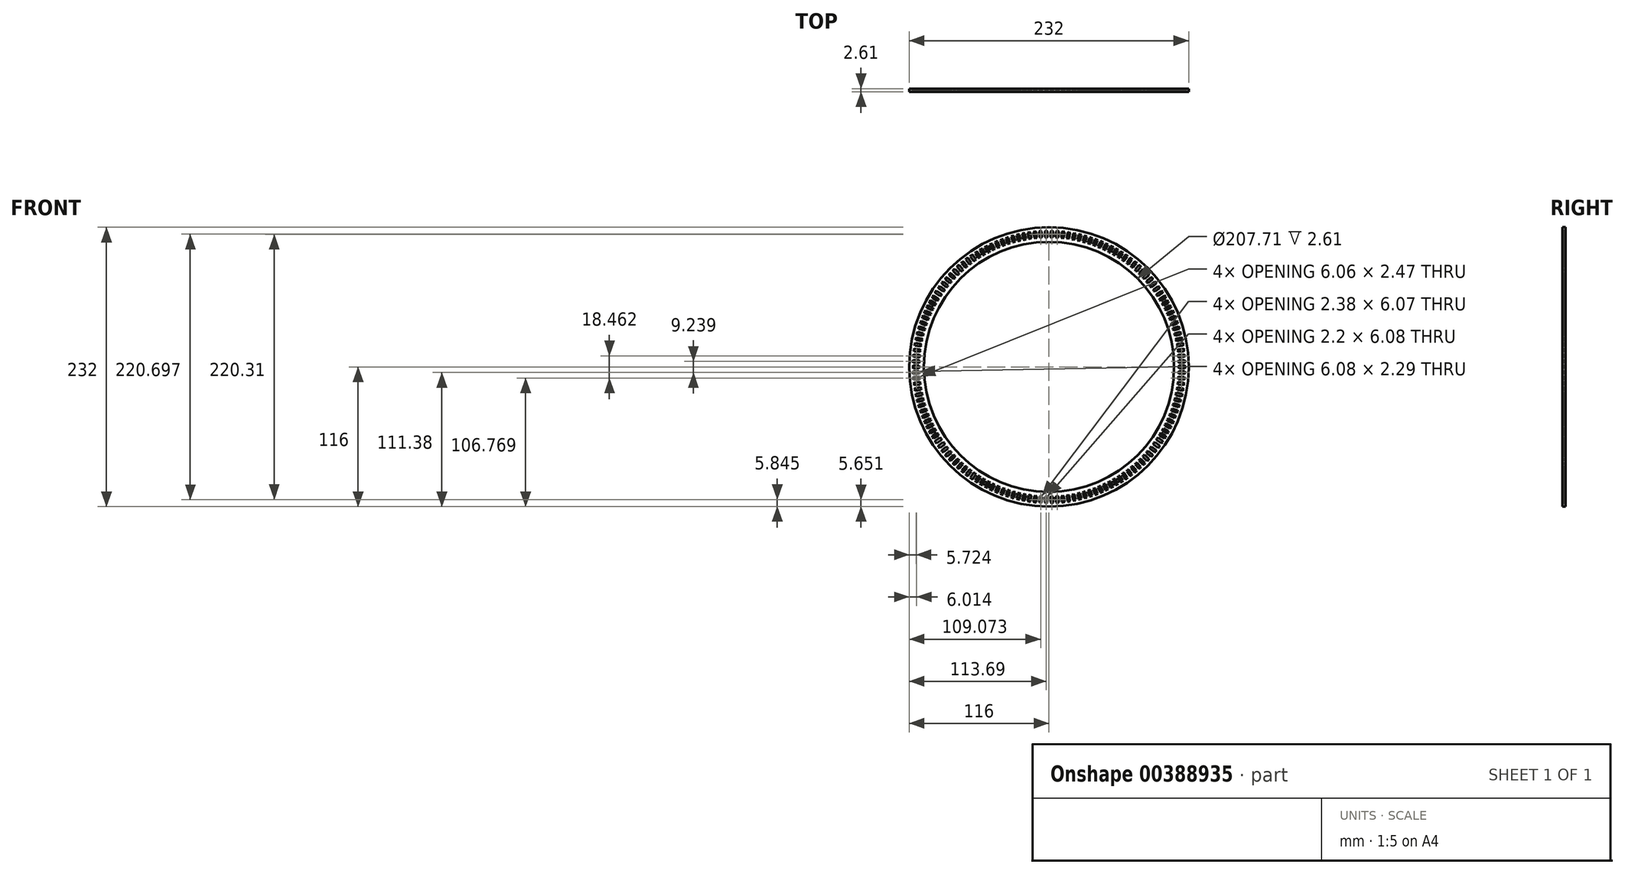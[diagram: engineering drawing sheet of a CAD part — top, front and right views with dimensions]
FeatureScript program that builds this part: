
annotation { "Feature Type Name" : "Feature", "Feature Type Description" : "" }
export const myFeature = defineFeature(function(context is Context, id is Id, definition is map)
    precondition{}
    {
        {
            var Q0;
            Q0=qCreatedBy(makeId("Front.planeOp"),FACE);
            var sketch = newSketch(context, id + "F0", { "sketchPlane" : qUnion([Q0])});
            skCircle(sketch, "E0", {"center": v(0, 0) * mm, "radius": 44.45 * mm});
            skCircle(sketch, "E1", {"center": v(0, 0) * mm, "radius": 39.8 * mm});
            skSolve(sketch);
        }
        {
            var Q0;
            Q0=makeQuery(id+"F0.imprint","IMPRINT",FACE,{"disambiguationData":[TD([[makeQuery(id+"F0.imprint","IMPRINT",EDGE,{"derivedFrom":sQuery(id+"F0.wireOp",EDGE,"E0")}),1.0]])]});
            extrude(context, id + "F1", {"entities" : qUnion([Q0]), "oppositeDirection" : true, "depth" : 1 * mm});
        }
        {
            var Q0;
            Q0=qCreatedBy(makeId("Front.planeOp"),FACE);
            var sketch = newSketch(context, id + "F2", { "sketchPlane" : qUnion([Q0])});
            skLineSegment(sketch, "E2", {"start": v(-43.11, 0.4) * mm, "end": v(-43.45, 0) * mm});
            skLineSegment(sketch, "E3", {"start": v(-41.42, 0.4) * mm, "end": v(-41.12, 0) * mm});
            skLineSegment(sketch, "E4", {"start": v(-41.12, 0) * mm, "end": v(-41.42, -0.4) * mm});
            skLineSegment(sketch, "E5", {"start": v(-43.45, 0) * mm, "end": v(-43.11, -0.4) * mm});
            skLineSegment(sketch, "E6", {"start": v(-43.11, 0.4) * mm, "end": v(-41.42, 0.4) * mm});
            skLineSegment(sketch, "E7", {"start": v(-41.42, -0.4) * mm, "end": v(-43.11, -0.4) * mm});
            skSolve(sketch);
        }
        {
            var Q0;
            Q0=qSketchRegion(id+"F2",true);
            extrude(context, id + "F3", {"entities" : qUnion([Q0]), "oppositeDirection" : true, "depth" : 1 * mm});
        }
        {
            var Q0;
            Q0=makeQuery(id+"F3.opExtrude","SWEPT_BODY",BODY,{"disambiguationData":[OSD([sQuery(id+"F2.wireOp",EDGE,"E2"),sQuery(id+"F2.wireOp",EDGE,"E3"),sQuery(id+"F2.wireOp",EDGE,"E4"),sQuery(id+"F2.wireOp",EDGE,"E5"),sQuery(id+"F2.wireOp",EDGE,"E6"),sQuery(id+"F2.wireOp",EDGE,"E7")])]});
            var Q1;
            Q1=sQuery(id+"F0.wireOp",EDGE,"E1");
            circularPattern(context, id + "F4", {"entities" : qUnion([Q0]), "axis" : qUnion([Q1]), "angle" : 360 * degree, "instanceCount" : 150, "equalSpace" : true});
        }
        {
            var Q0;
            Q0=makeQuery(id+"F4.opPattern","COPY",BODY,{"derivedFrom":makeQuery(id+"F3.opExtrude","SWEPT_BODY",BODY,{"disambiguationData":[OSD([sQuery(id+"F2.wireOp",EDGE,"E2"),sQuery(id+"F2.wireOp",EDGE,"E3"),sQuery(id+"F2.wireOp",EDGE,"E4"),sQuery(id+"F2.wireOp",EDGE,"E5"),sQuery(id+"F2.wireOp",EDGE,"E6"),sQuery(id+"F2.wireOp",EDGE,"E7")])]}),"instanceName":"5"});
            var Q1;
            Q1=makeQuery(id+"F4.opPattern","COPY",BODY,{"derivedFrom":makeQuery(id+"F3.opExtrude","SWEPT_BODY",BODY,{"disambiguationData":[OSD([sQuery(id+"F2.wireOp",EDGE,"E2"),sQuery(id+"F2.wireOp",EDGE,"E3"),sQuery(id+"F2.wireOp",EDGE,"E4"),sQuery(id+"F2.wireOp",EDGE,"E5"),sQuery(id+"F2.wireOp",EDGE,"E6"),sQuery(id+"F2.wireOp",EDGE,"E7")])]}),"instanceName":"6"});
            var Q2;
            Q2=makeQuery(id+"F4.opPattern","COPY",BODY,{"derivedFrom":makeQuery(id+"F3.opExtrude","SWEPT_BODY",BODY,{"disambiguationData":[OSD([sQuery(id+"F2.wireOp",EDGE,"E2"),sQuery(id+"F2.wireOp",EDGE,"E3"),sQuery(id+"F2.wireOp",EDGE,"E4"),sQuery(id+"F2.wireOp",EDGE,"E5"),sQuery(id+"F2.wireOp",EDGE,"E6"),sQuery(id+"F2.wireOp",EDGE,"E7")])]}),"instanceName":"4"});
            var Q3;
            Q3=makeQuery(id+"F4.opPattern","COPY",BODY,{"derivedFrom":makeQuery(id+"F3.opExtrude","SWEPT_BODY",BODY,{"disambiguationData":[OSD([sQuery(id+"F2.wireOp",EDGE,"E2"),sQuery(id+"F2.wireOp",EDGE,"E3"),sQuery(id+"F2.wireOp",EDGE,"E4"),sQuery(id+"F2.wireOp",EDGE,"E5"),sQuery(id+"F2.wireOp",EDGE,"E6"),sQuery(id+"F2.wireOp",EDGE,"E7")])]}),"instanceName":"23"});
            var Q4;
            Q4=makeQuery(id+"F4.opPattern","COPY",BODY,{"derivedFrom":makeQuery(id+"F3.opExtrude","SWEPT_BODY",BODY,{"disambiguationData":[OSD([sQuery(id+"F2.wireOp",EDGE,"E2"),sQuery(id+"F2.wireOp",EDGE,"E3"),sQuery(id+"F2.wireOp",EDGE,"E4"),sQuery(id+"F2.wireOp",EDGE,"E5"),sQuery(id+"F2.wireOp",EDGE,"E6"),sQuery(id+"F2.wireOp",EDGE,"E7")])]}),"instanceName":"21"});
            var Q5;
            Q5=makeQuery(id+"F4.opPattern","COPY",BODY,{"derivedFrom":makeQuery(id+"F3.opExtrude","SWEPT_BODY",BODY,{"disambiguationData":[OSD([sQuery(id+"F2.wireOp",EDGE,"E2"),sQuery(id+"F2.wireOp",EDGE,"E3"),sQuery(id+"F2.wireOp",EDGE,"E4"),sQuery(id+"F2.wireOp",EDGE,"E5"),sQuery(id+"F2.wireOp",EDGE,"E6"),sQuery(id+"F2.wireOp",EDGE,"E7")])]}),"instanceName":"24"});
            var Q6;
            Q6=makeQuery(id+"F4.opPattern","COPY",BODY,{"derivedFrom":makeQuery(id+"F3.opExtrude","SWEPT_BODY",BODY,{"disambiguationData":[OSD([sQuery(id+"F2.wireOp",EDGE,"E2"),sQuery(id+"F2.wireOp",EDGE,"E3"),sQuery(id+"F2.wireOp",EDGE,"E4"),sQuery(id+"F2.wireOp",EDGE,"E5"),sQuery(id+"F2.wireOp",EDGE,"E6"),sQuery(id+"F2.wireOp",EDGE,"E7")])]}),"instanceName":"22"});
            var Q7;
            Q7=makeQuery(id+"F4.opPattern","COPY",BODY,{"derivedFrom":makeQuery(id+"F3.opExtrude","SWEPT_BODY",BODY,{"disambiguationData":[OSD([sQuery(id+"F2.wireOp",EDGE,"E2"),sQuery(id+"F2.wireOp",EDGE,"E3"),sQuery(id+"F2.wireOp",EDGE,"E4"),sQuery(id+"F2.wireOp",EDGE,"E5"),sQuery(id+"F2.wireOp",EDGE,"E6"),sQuery(id+"F2.wireOp",EDGE,"E7")])]}),"instanceName":"20"});
            var Q8;
            Q8=makeQuery(id+"F4.opPattern","COPY",BODY,{"derivedFrom":makeQuery(id+"F3.opExtrude","SWEPT_BODY",BODY,{"disambiguationData":[OSD([sQuery(id+"F2.wireOp",EDGE,"E2"),sQuery(id+"F2.wireOp",EDGE,"E3"),sQuery(id+"F2.wireOp",EDGE,"E4"),sQuery(id+"F2.wireOp",EDGE,"E5"),sQuery(id+"F2.wireOp",EDGE,"E6"),sQuery(id+"F2.wireOp",EDGE,"E7")])]}),"instanceName":"19"});
            var Q9;
            Q9=makeQuery(id+"F4.opPattern","COPY",BODY,{"derivedFrom":makeQuery(id+"F3.opExtrude","SWEPT_BODY",BODY,{"disambiguationData":[OSD([sQuery(id+"F2.wireOp",EDGE,"E2"),sQuery(id+"F2.wireOp",EDGE,"E3"),sQuery(id+"F2.wireOp",EDGE,"E4"),sQuery(id+"F2.wireOp",EDGE,"E5"),sQuery(id+"F2.wireOp",EDGE,"E6"),sQuery(id+"F2.wireOp",EDGE,"E7")])]}),"instanceName":"18"});
            var Q10;
            Q10=makeQuery(id+"F4.opPattern","COPY",BODY,{"derivedFrom":makeQuery(id+"F3.opExtrude","SWEPT_BODY",BODY,{"disambiguationData":[OSD([sQuery(id+"F2.wireOp",EDGE,"E2"),sQuery(id+"F2.wireOp",EDGE,"E3"),sQuery(id+"F2.wireOp",EDGE,"E4"),sQuery(id+"F2.wireOp",EDGE,"E5"),sQuery(id+"F2.wireOp",EDGE,"E6"),sQuery(id+"F2.wireOp",EDGE,"E7")])]}),"instanceName":"17"});
            var Q11;
            Q11=makeQuery(id+"F4.opPattern","COPY",BODY,{"derivedFrom":makeQuery(id+"F3.opExtrude","SWEPT_BODY",BODY,{"disambiguationData":[OSD([sQuery(id+"F2.wireOp",EDGE,"E2"),sQuery(id+"F2.wireOp",EDGE,"E3"),sQuery(id+"F2.wireOp",EDGE,"E4"),sQuery(id+"F2.wireOp",EDGE,"E5"),sQuery(id+"F2.wireOp",EDGE,"E6"),sQuery(id+"F2.wireOp",EDGE,"E7")])]}),"instanceName":"16"});
            var Q12;
            Q12=makeQuery(id+"F4.opPattern","COPY",BODY,{"derivedFrom":makeQuery(id+"F3.opExtrude","SWEPT_BODY",BODY,{"disambiguationData":[OSD([sQuery(id+"F2.wireOp",EDGE,"E2"),sQuery(id+"F2.wireOp",EDGE,"E3"),sQuery(id+"F2.wireOp",EDGE,"E4"),sQuery(id+"F2.wireOp",EDGE,"E5"),sQuery(id+"F2.wireOp",EDGE,"E6"),sQuery(id+"F2.wireOp",EDGE,"E7")])]}),"instanceName":"15"});
            var Q13;
            Q13=makeQuery(id+"F4.opPattern","COPY",BODY,{"derivedFrom":makeQuery(id+"F3.opExtrude","SWEPT_BODY",BODY,{"disambiguationData":[OSD([sQuery(id+"F2.wireOp",EDGE,"E2"),sQuery(id+"F2.wireOp",EDGE,"E3"),sQuery(id+"F2.wireOp",EDGE,"E4"),sQuery(id+"F2.wireOp",EDGE,"E5"),sQuery(id+"F2.wireOp",EDGE,"E6"),sQuery(id+"F2.wireOp",EDGE,"E7")])]}),"instanceName":"14"});
            var Q14;
            Q14=makeQuery(id+"F4.opPattern","COPY",BODY,{"derivedFrom":makeQuery(id+"F3.opExtrude","SWEPT_BODY",BODY,{"disambiguationData":[OSD([sQuery(id+"F2.wireOp",EDGE,"E2"),sQuery(id+"F2.wireOp",EDGE,"E3"),sQuery(id+"F2.wireOp",EDGE,"E4"),sQuery(id+"F2.wireOp",EDGE,"E5"),sQuery(id+"F2.wireOp",EDGE,"E6"),sQuery(id+"F2.wireOp",EDGE,"E7")])]}),"instanceName":"13"});
            var Q15;
            Q15=makeQuery(id+"F4.opPattern","COPY",BODY,{"derivedFrom":makeQuery(id+"F3.opExtrude","SWEPT_BODY",BODY,{"disambiguationData":[OSD([sQuery(id+"F2.wireOp",EDGE,"E2"),sQuery(id+"F2.wireOp",EDGE,"E3"),sQuery(id+"F2.wireOp",EDGE,"E4"),sQuery(id+"F2.wireOp",EDGE,"E5"),sQuery(id+"F2.wireOp",EDGE,"E6"),sQuery(id+"F2.wireOp",EDGE,"E7")])]}),"instanceName":"12"});
            var Q16;
            Q16=makeQuery(id+"F4.opPattern","COPY",BODY,{"derivedFrom":makeQuery(id+"F3.opExtrude","SWEPT_BODY",BODY,{"disambiguationData":[OSD([sQuery(id+"F2.wireOp",EDGE,"E2"),sQuery(id+"F2.wireOp",EDGE,"E3"),sQuery(id+"F2.wireOp",EDGE,"E4"),sQuery(id+"F2.wireOp",EDGE,"E5"),sQuery(id+"F2.wireOp",EDGE,"E6"),sQuery(id+"F2.wireOp",EDGE,"E7")])]}),"instanceName":"11"});
            var Q17;
            Q17=makeQuery(id+"F4.opPattern","COPY",BODY,{"derivedFrom":makeQuery(id+"F3.opExtrude","SWEPT_BODY",BODY,{"disambiguationData":[OSD([sQuery(id+"F2.wireOp",EDGE,"E2"),sQuery(id+"F2.wireOp",EDGE,"E3"),sQuery(id+"F2.wireOp",EDGE,"E4"),sQuery(id+"F2.wireOp",EDGE,"E5"),sQuery(id+"F2.wireOp",EDGE,"E6"),sQuery(id+"F2.wireOp",EDGE,"E7")])]}),"instanceName":"10"});
            var Q18;
            Q18=makeQuery(id+"F4.opPattern","COPY",BODY,{"derivedFrom":makeQuery(id+"F3.opExtrude","SWEPT_BODY",BODY,{"disambiguationData":[OSD([sQuery(id+"F2.wireOp",EDGE,"E2"),sQuery(id+"F2.wireOp",EDGE,"E3"),sQuery(id+"F2.wireOp",EDGE,"E4"),sQuery(id+"F2.wireOp",EDGE,"E5"),sQuery(id+"F2.wireOp",EDGE,"E6"),sQuery(id+"F2.wireOp",EDGE,"E7")])]}),"instanceName":"9"});
            var Q19;
            Q19=makeQuery(id+"F4.opPattern","COPY",BODY,{"derivedFrom":makeQuery(id+"F3.opExtrude","SWEPT_BODY",BODY,{"disambiguationData":[OSD([sQuery(id+"F2.wireOp",EDGE,"E2"),sQuery(id+"F2.wireOp",EDGE,"E3"),sQuery(id+"F2.wireOp",EDGE,"E4"),sQuery(id+"F2.wireOp",EDGE,"E5"),sQuery(id+"F2.wireOp",EDGE,"E6"),sQuery(id+"F2.wireOp",EDGE,"E7")])]}),"instanceName":"8"});
            var Q20;
            Q20=makeQuery(id+"F4.opPattern","COPY",BODY,{"derivedFrom":makeQuery(id+"F3.opExtrude","SWEPT_BODY",BODY,{"disambiguationData":[OSD([sQuery(id+"F2.wireOp",EDGE,"E2"),sQuery(id+"F2.wireOp",EDGE,"E3"),sQuery(id+"F2.wireOp",EDGE,"E4"),sQuery(id+"F2.wireOp",EDGE,"E5"),sQuery(id+"F2.wireOp",EDGE,"E6"),sQuery(id+"F2.wireOp",EDGE,"E7")])]}),"instanceName":"7"});
            var Q21;
            Q21=makeQuery(id+"F4.opPattern","COPY",BODY,{"derivedFrom":makeQuery(id+"F3.opExtrude","SWEPT_BODY",BODY,{"disambiguationData":[OSD([sQuery(id+"F2.wireOp",EDGE,"E2"),sQuery(id+"F2.wireOp",EDGE,"E3"),sQuery(id+"F2.wireOp",EDGE,"E4"),sQuery(id+"F2.wireOp",EDGE,"E5"),sQuery(id+"F2.wireOp",EDGE,"E6"),sQuery(id+"F2.wireOp",EDGE,"E7")])]}),"instanceName":"1"});
            var Q22;
            Q22=makeQuery(id+"F4.opPattern","COPY",BODY,{"derivedFrom":makeQuery(id+"F3.opExtrude","SWEPT_BODY",BODY,{"disambiguationData":[OSD([sQuery(id+"F2.wireOp",EDGE,"E2"),sQuery(id+"F2.wireOp",EDGE,"E3"),sQuery(id+"F2.wireOp",EDGE,"E4"),sQuery(id+"F2.wireOp",EDGE,"E5"),sQuery(id+"F2.wireOp",EDGE,"E6"),sQuery(id+"F2.wireOp",EDGE,"E7")])]}),"instanceName":"3"});
            var Q23;
            Q23=makeQuery(id+"F4.opPattern","COPY",BODY,{"derivedFrom":makeQuery(id+"F3.opExtrude","SWEPT_BODY",BODY,{"disambiguationData":[OSD([sQuery(id+"F2.wireOp",EDGE,"E2"),sQuery(id+"F2.wireOp",EDGE,"E3"),sQuery(id+"F2.wireOp",EDGE,"E4"),sQuery(id+"F2.wireOp",EDGE,"E5"),sQuery(id+"F2.wireOp",EDGE,"E6"),sQuery(id+"F2.wireOp",EDGE,"E7")])]}),"instanceName":"2"});
            var Q24;
            Q24=makeQuery(id+"F3.opExtrude","SWEPT_BODY",BODY,{"disambiguationData":[OSD([sQuery(id+"F2.wireOp",EDGE,"E2"),sQuery(id+"F2.wireOp",EDGE,"E3"),sQuery(id+"F2.wireOp",EDGE,"E4"),sQuery(id+"F2.wireOp",EDGE,"E5"),sQuery(id+"F2.wireOp",EDGE,"E6"),sQuery(id+"F2.wireOp",EDGE,"E7")])]});
            var Q25;
            Q25=makeQuery(id+"F4.opPattern","COPY",BODY,{"derivedFrom":makeQuery(id+"F3.opExtrude","SWEPT_BODY",BODY,{"disambiguationData":[OSD([sQuery(id+"F2.wireOp",EDGE,"E2"),sQuery(id+"F2.wireOp",EDGE,"E3"),sQuery(id+"F2.wireOp",EDGE,"E4"),sQuery(id+"F2.wireOp",EDGE,"E5"),sQuery(id+"F2.wireOp",EDGE,"E6"),sQuery(id+"F2.wireOp",EDGE,"E7")])]}),"instanceName":"149"});
            var Q26;
            Q26=makeQuery(id+"F4.opPattern","COPY",BODY,{"derivedFrom":makeQuery(id+"F3.opExtrude","SWEPT_BODY",BODY,{"disambiguationData":[OSD([sQuery(id+"F2.wireOp",EDGE,"E2"),sQuery(id+"F2.wireOp",EDGE,"E3"),sQuery(id+"F2.wireOp",EDGE,"E4"),sQuery(id+"F2.wireOp",EDGE,"E5"),sQuery(id+"F2.wireOp",EDGE,"E6"),sQuery(id+"F2.wireOp",EDGE,"E7")])]}),"instanceName":"148"});
            var Q27;
            Q27=makeQuery(id+"F4.opPattern","COPY",BODY,{"derivedFrom":makeQuery(id+"F3.opExtrude","SWEPT_BODY",BODY,{"disambiguationData":[OSD([sQuery(id+"F2.wireOp",EDGE,"E2"),sQuery(id+"F2.wireOp",EDGE,"E3"),sQuery(id+"F2.wireOp",EDGE,"E4"),sQuery(id+"F2.wireOp",EDGE,"E5"),sQuery(id+"F2.wireOp",EDGE,"E6"),sQuery(id+"F2.wireOp",EDGE,"E7")])]}),"instanceName":"147"});
            var Q28;
            Q28=makeQuery(id+"F4.opPattern","COPY",BODY,{"derivedFrom":makeQuery(id+"F3.opExtrude","SWEPT_BODY",BODY,{"disambiguationData":[OSD([sQuery(id+"F2.wireOp",EDGE,"E2"),sQuery(id+"F2.wireOp",EDGE,"E3"),sQuery(id+"F2.wireOp",EDGE,"E4"),sQuery(id+"F2.wireOp",EDGE,"E5"),sQuery(id+"F2.wireOp",EDGE,"E6"),sQuery(id+"F2.wireOp",EDGE,"E7")])]}),"instanceName":"25"});
            var Q29;
            Q29=makeQuery(id+"F4.opPattern","COPY",BODY,{"derivedFrom":makeQuery(id+"F3.opExtrude","SWEPT_BODY",BODY,{"disambiguationData":[OSD([sQuery(id+"F2.wireOp",EDGE,"E2"),sQuery(id+"F2.wireOp",EDGE,"E3"),sQuery(id+"F2.wireOp",EDGE,"E4"),sQuery(id+"F2.wireOp",EDGE,"E5"),sQuery(id+"F2.wireOp",EDGE,"E6"),sQuery(id+"F2.wireOp",EDGE,"E7")])]}),"instanceName":"26"});
            var Q30;
            Q30=makeQuery(id+"F4.opPattern","COPY",BODY,{"derivedFrom":makeQuery(id+"F3.opExtrude","SWEPT_BODY",BODY,{"disambiguationData":[OSD([sQuery(id+"F2.wireOp",EDGE,"E2"),sQuery(id+"F2.wireOp",EDGE,"E3"),sQuery(id+"F2.wireOp",EDGE,"E4"),sQuery(id+"F2.wireOp",EDGE,"E5"),sQuery(id+"F2.wireOp",EDGE,"E6"),sQuery(id+"F2.wireOp",EDGE,"E7")])]}),"instanceName":"27"});
            var Q31;
            Q31=makeQuery(id+"F4.opPattern","COPY",BODY,{"derivedFrom":makeQuery(id+"F3.opExtrude","SWEPT_BODY",BODY,{"disambiguationData":[OSD([sQuery(id+"F2.wireOp",EDGE,"E2"),sQuery(id+"F2.wireOp",EDGE,"E3"),sQuery(id+"F2.wireOp",EDGE,"E4"),sQuery(id+"F2.wireOp",EDGE,"E5"),sQuery(id+"F2.wireOp",EDGE,"E6"),sQuery(id+"F2.wireOp",EDGE,"E7")])]}),"instanceName":"28"});
            var Q32;
            Q32=makeQuery(id+"F4.opPattern","COPY",BODY,{"derivedFrom":makeQuery(id+"F3.opExtrude","SWEPT_BODY",BODY,{"disambiguationData":[OSD([sQuery(id+"F2.wireOp",EDGE,"E2"),sQuery(id+"F2.wireOp",EDGE,"E3"),sQuery(id+"F2.wireOp",EDGE,"E4"),sQuery(id+"F2.wireOp",EDGE,"E5"),sQuery(id+"F2.wireOp",EDGE,"E6"),sQuery(id+"F2.wireOp",EDGE,"E7")])]}),"instanceName":"29"});
            var Q33;
            Q33=makeQuery(id+"F4.opPattern","COPY",BODY,{"derivedFrom":makeQuery(id+"F3.opExtrude","SWEPT_BODY",BODY,{"disambiguationData":[OSD([sQuery(id+"F2.wireOp",EDGE,"E2"),sQuery(id+"F2.wireOp",EDGE,"E3"),sQuery(id+"F2.wireOp",EDGE,"E4"),sQuery(id+"F2.wireOp",EDGE,"E5"),sQuery(id+"F2.wireOp",EDGE,"E6"),sQuery(id+"F2.wireOp",EDGE,"E7")])]}),"instanceName":"30"});
            var Q34;
            Q34=makeQuery(id+"F4.opPattern","COPY",BODY,{"derivedFrom":makeQuery(id+"F3.opExtrude","SWEPT_BODY",BODY,{"disambiguationData":[OSD([sQuery(id+"F2.wireOp",EDGE,"E2"),sQuery(id+"F2.wireOp",EDGE,"E3"),sQuery(id+"F2.wireOp",EDGE,"E4"),sQuery(id+"F2.wireOp",EDGE,"E5"),sQuery(id+"F2.wireOp",EDGE,"E6"),sQuery(id+"F2.wireOp",EDGE,"E7")])]}),"instanceName":"31"});
            var Q35;
            Q35=makeQuery(id+"F4.opPattern","COPY",BODY,{"derivedFrom":makeQuery(id+"F3.opExtrude","SWEPT_BODY",BODY,{"disambiguationData":[OSD([sQuery(id+"F2.wireOp",EDGE,"E2"),sQuery(id+"F2.wireOp",EDGE,"E3"),sQuery(id+"F2.wireOp",EDGE,"E4"),sQuery(id+"F2.wireOp",EDGE,"E5"),sQuery(id+"F2.wireOp",EDGE,"E6"),sQuery(id+"F2.wireOp",EDGE,"E7")])]}),"instanceName":"32"});
            var Q36;
            Q36=makeQuery(id+"F4.opPattern","COPY",BODY,{"derivedFrom":makeQuery(id+"F3.opExtrude","SWEPT_BODY",BODY,{"disambiguationData":[OSD([sQuery(id+"F2.wireOp",EDGE,"E2"),sQuery(id+"F2.wireOp",EDGE,"E3"),sQuery(id+"F2.wireOp",EDGE,"E4"),sQuery(id+"F2.wireOp",EDGE,"E5"),sQuery(id+"F2.wireOp",EDGE,"E6"),sQuery(id+"F2.wireOp",EDGE,"E7")])]}),"instanceName":"33"});
            var Q37;
            Q37=makeQuery(id+"F4.opPattern","COPY",BODY,{"derivedFrom":makeQuery(id+"F3.opExtrude","SWEPT_BODY",BODY,{"disambiguationData":[OSD([sQuery(id+"F2.wireOp",EDGE,"E2"),sQuery(id+"F2.wireOp",EDGE,"E3"),sQuery(id+"F2.wireOp",EDGE,"E4"),sQuery(id+"F2.wireOp",EDGE,"E5"),sQuery(id+"F2.wireOp",EDGE,"E6"),sQuery(id+"F2.wireOp",EDGE,"E7")])]}),"instanceName":"34"});
            var Q38;
            Q38=makeQuery(id+"F4.opPattern","COPY",BODY,{"derivedFrom":makeQuery(id+"F3.opExtrude","SWEPT_BODY",BODY,{"disambiguationData":[OSD([sQuery(id+"F2.wireOp",EDGE,"E2"),sQuery(id+"F2.wireOp",EDGE,"E3"),sQuery(id+"F2.wireOp",EDGE,"E4"),sQuery(id+"F2.wireOp",EDGE,"E5"),sQuery(id+"F2.wireOp",EDGE,"E6"),sQuery(id+"F2.wireOp",EDGE,"E7")])]}),"instanceName":"35"});
            var Q39;
            Q39=makeQuery(id+"F4.opPattern","COPY",BODY,{"derivedFrom":makeQuery(id+"F3.opExtrude","SWEPT_BODY",BODY,{"disambiguationData":[OSD([sQuery(id+"F2.wireOp",EDGE,"E2"),sQuery(id+"F2.wireOp",EDGE,"E3"),sQuery(id+"F2.wireOp",EDGE,"E4"),sQuery(id+"F2.wireOp",EDGE,"E5"),sQuery(id+"F2.wireOp",EDGE,"E6"),sQuery(id+"F2.wireOp",EDGE,"E7")])]}),"instanceName":"36"});
            var Q40;
            Q40=makeQuery(id+"F4.opPattern","COPY",BODY,{"derivedFrom":makeQuery(id+"F3.opExtrude","SWEPT_BODY",BODY,{"disambiguationData":[OSD([sQuery(id+"F2.wireOp",EDGE,"E2"),sQuery(id+"F2.wireOp",EDGE,"E3"),sQuery(id+"F2.wireOp",EDGE,"E4"),sQuery(id+"F2.wireOp",EDGE,"E5"),sQuery(id+"F2.wireOp",EDGE,"E6"),sQuery(id+"F2.wireOp",EDGE,"E7")])]}),"instanceName":"37"});
            var Q41;
            Q41=makeQuery(id+"F4.opPattern","COPY",BODY,{"derivedFrom":makeQuery(id+"F3.opExtrude","SWEPT_BODY",BODY,{"disambiguationData":[OSD([sQuery(id+"F2.wireOp",EDGE,"E2"),sQuery(id+"F2.wireOp",EDGE,"E3"),sQuery(id+"F2.wireOp",EDGE,"E4"),sQuery(id+"F2.wireOp",EDGE,"E5"),sQuery(id+"F2.wireOp",EDGE,"E6"),sQuery(id+"F2.wireOp",EDGE,"E7")])]}),"instanceName":"38"});
            var Q42;
            Q42=makeQuery(id+"F4.opPattern","COPY",BODY,{"derivedFrom":makeQuery(id+"F3.opExtrude","SWEPT_BODY",BODY,{"disambiguationData":[OSD([sQuery(id+"F2.wireOp",EDGE,"E2"),sQuery(id+"F2.wireOp",EDGE,"E3"),sQuery(id+"F2.wireOp",EDGE,"E4"),sQuery(id+"F2.wireOp",EDGE,"E5"),sQuery(id+"F2.wireOp",EDGE,"E6"),sQuery(id+"F2.wireOp",EDGE,"E7")])]}),"instanceName":"39"});
            var Q43;
            Q43=makeQuery(id+"F4.opPattern","COPY",BODY,{"derivedFrom":makeQuery(id+"F3.opExtrude","SWEPT_BODY",BODY,{"disambiguationData":[OSD([sQuery(id+"F2.wireOp",EDGE,"E2"),sQuery(id+"F2.wireOp",EDGE,"E3"),sQuery(id+"F2.wireOp",EDGE,"E4"),sQuery(id+"F2.wireOp",EDGE,"E5"),sQuery(id+"F2.wireOp",EDGE,"E6"),sQuery(id+"F2.wireOp",EDGE,"E7")])]}),"instanceName":"40"});
            var Q44;
            Q44=makeQuery(id+"F4.opPattern","COPY",BODY,{"derivedFrom":makeQuery(id+"F3.opExtrude","SWEPT_BODY",BODY,{"disambiguationData":[OSD([sQuery(id+"F2.wireOp",EDGE,"E2"),sQuery(id+"F2.wireOp",EDGE,"E3"),sQuery(id+"F2.wireOp",EDGE,"E4"),sQuery(id+"F2.wireOp",EDGE,"E5"),sQuery(id+"F2.wireOp",EDGE,"E6"),sQuery(id+"F2.wireOp",EDGE,"E7")])]}),"instanceName":"41"});
            var Q45;
            Q45=makeQuery(id+"F4.opPattern","COPY",BODY,{"derivedFrom":makeQuery(id+"F3.opExtrude","SWEPT_BODY",BODY,{"disambiguationData":[OSD([sQuery(id+"F2.wireOp",EDGE,"E2"),sQuery(id+"F2.wireOp",EDGE,"E3"),sQuery(id+"F2.wireOp",EDGE,"E4"),sQuery(id+"F2.wireOp",EDGE,"E5"),sQuery(id+"F2.wireOp",EDGE,"E6"),sQuery(id+"F2.wireOp",EDGE,"E7")])]}),"instanceName":"42"});
            var Q46;
            Q46=makeQuery(id+"F4.opPattern","COPY",BODY,{"derivedFrom":makeQuery(id+"F3.opExtrude","SWEPT_BODY",BODY,{"disambiguationData":[OSD([sQuery(id+"F2.wireOp",EDGE,"E2"),sQuery(id+"F2.wireOp",EDGE,"E3"),sQuery(id+"F2.wireOp",EDGE,"E4"),sQuery(id+"F2.wireOp",EDGE,"E5"),sQuery(id+"F2.wireOp",EDGE,"E6"),sQuery(id+"F2.wireOp",EDGE,"E7")])]}),"instanceName":"43"});
            var Q47;
            Q47=makeQuery(id+"F4.opPattern","COPY",BODY,{"derivedFrom":makeQuery(id+"F3.opExtrude","SWEPT_BODY",BODY,{"disambiguationData":[OSD([sQuery(id+"F2.wireOp",EDGE,"E2"),sQuery(id+"F2.wireOp",EDGE,"E3"),sQuery(id+"F2.wireOp",EDGE,"E4"),sQuery(id+"F2.wireOp",EDGE,"E5"),sQuery(id+"F2.wireOp",EDGE,"E6"),sQuery(id+"F2.wireOp",EDGE,"E7")])]}),"instanceName":"44"});
            var Q48;
            Q48=makeQuery(id+"F4.opPattern","COPY",BODY,{"derivedFrom":makeQuery(id+"F3.opExtrude","SWEPT_BODY",BODY,{"disambiguationData":[OSD([sQuery(id+"F2.wireOp",EDGE,"E2"),sQuery(id+"F2.wireOp",EDGE,"E3"),sQuery(id+"F2.wireOp",EDGE,"E4"),sQuery(id+"F2.wireOp",EDGE,"E5"),sQuery(id+"F2.wireOp",EDGE,"E6"),sQuery(id+"F2.wireOp",EDGE,"E7")])]}),"instanceName":"45"});
            var Q49;
            Q49=makeQuery(id+"F4.opPattern","COPY",BODY,{"derivedFrom":makeQuery(id+"F3.opExtrude","SWEPT_BODY",BODY,{"disambiguationData":[OSD([sQuery(id+"F2.wireOp",EDGE,"E2"),sQuery(id+"F2.wireOp",EDGE,"E3"),sQuery(id+"F2.wireOp",EDGE,"E4"),sQuery(id+"F2.wireOp",EDGE,"E5"),sQuery(id+"F2.wireOp",EDGE,"E6"),sQuery(id+"F2.wireOp",EDGE,"E7")])]}),"instanceName":"46"});
            var Q50;
            Q50=makeQuery(id+"F4.opPattern","COPY",BODY,{"derivedFrom":makeQuery(id+"F3.opExtrude","SWEPT_BODY",BODY,{"disambiguationData":[OSD([sQuery(id+"F2.wireOp",EDGE,"E2"),sQuery(id+"F2.wireOp",EDGE,"E3"),sQuery(id+"F2.wireOp",EDGE,"E4"),sQuery(id+"F2.wireOp",EDGE,"E5"),sQuery(id+"F2.wireOp",EDGE,"E6"),sQuery(id+"F2.wireOp",EDGE,"E7")])]}),"instanceName":"47"});
            var Q51;
            Q51=makeQuery(id+"F4.opPattern","COPY",BODY,{"derivedFrom":makeQuery(id+"F3.opExtrude","SWEPT_BODY",BODY,{"disambiguationData":[OSD([sQuery(id+"F2.wireOp",EDGE,"E2"),sQuery(id+"F2.wireOp",EDGE,"E3"),sQuery(id+"F2.wireOp",EDGE,"E4"),sQuery(id+"F2.wireOp",EDGE,"E5"),sQuery(id+"F2.wireOp",EDGE,"E6"),sQuery(id+"F2.wireOp",EDGE,"E7")])]}),"instanceName":"48"});
            var Q52;
            Q52=makeQuery(id+"F4.opPattern","COPY",BODY,{"derivedFrom":makeQuery(id+"F3.opExtrude","SWEPT_BODY",BODY,{"disambiguationData":[OSD([sQuery(id+"F2.wireOp",EDGE,"E2"),sQuery(id+"F2.wireOp",EDGE,"E3"),sQuery(id+"F2.wireOp",EDGE,"E4"),sQuery(id+"F2.wireOp",EDGE,"E5"),sQuery(id+"F2.wireOp",EDGE,"E6"),sQuery(id+"F2.wireOp",EDGE,"E7")])]}),"instanceName":"49"});
            var Q53;
            Q53=makeQuery(id+"F4.opPattern","COPY",BODY,{"derivedFrom":makeQuery(id+"F3.opExtrude","SWEPT_BODY",BODY,{"disambiguationData":[OSD([sQuery(id+"F2.wireOp",EDGE,"E2"),sQuery(id+"F2.wireOp",EDGE,"E3"),sQuery(id+"F2.wireOp",EDGE,"E4"),sQuery(id+"F2.wireOp",EDGE,"E5"),sQuery(id+"F2.wireOp",EDGE,"E6"),sQuery(id+"F2.wireOp",EDGE,"E7")])]}),"instanceName":"50"});
            var Q54;
            Q54=makeQuery(id+"F4.opPattern","COPY",BODY,{"derivedFrom":makeQuery(id+"F3.opExtrude","SWEPT_BODY",BODY,{"disambiguationData":[OSD([sQuery(id+"F2.wireOp",EDGE,"E2"),sQuery(id+"F2.wireOp",EDGE,"E3"),sQuery(id+"F2.wireOp",EDGE,"E4"),sQuery(id+"F2.wireOp",EDGE,"E5"),sQuery(id+"F2.wireOp",EDGE,"E6"),sQuery(id+"F2.wireOp",EDGE,"E7")])]}),"instanceName":"51"});
            var Q55;
            Q55=makeQuery(id+"F4.opPattern","COPY",BODY,{"derivedFrom":makeQuery(id+"F3.opExtrude","SWEPT_BODY",BODY,{"disambiguationData":[OSD([sQuery(id+"F2.wireOp",EDGE,"E2"),sQuery(id+"F2.wireOp",EDGE,"E3"),sQuery(id+"F2.wireOp",EDGE,"E4"),sQuery(id+"F2.wireOp",EDGE,"E5"),sQuery(id+"F2.wireOp",EDGE,"E6"),sQuery(id+"F2.wireOp",EDGE,"E7")])]}),"instanceName":"52"});
            var Q56;
            Q56=makeQuery(id+"F4.opPattern","COPY",BODY,{"derivedFrom":makeQuery(id+"F3.opExtrude","SWEPT_BODY",BODY,{"disambiguationData":[OSD([sQuery(id+"F2.wireOp",EDGE,"E2"),sQuery(id+"F2.wireOp",EDGE,"E3"),sQuery(id+"F2.wireOp",EDGE,"E4"),sQuery(id+"F2.wireOp",EDGE,"E5"),sQuery(id+"F2.wireOp",EDGE,"E6"),sQuery(id+"F2.wireOp",EDGE,"E7")])]}),"instanceName":"53"});
            var Q57;
            Q57=makeQuery(id+"F4.opPattern","COPY",BODY,{"derivedFrom":makeQuery(id+"F3.opExtrude","SWEPT_BODY",BODY,{"disambiguationData":[OSD([sQuery(id+"F2.wireOp",EDGE,"E2"),sQuery(id+"F2.wireOp",EDGE,"E3"),sQuery(id+"F2.wireOp",EDGE,"E4"),sQuery(id+"F2.wireOp",EDGE,"E5"),sQuery(id+"F2.wireOp",EDGE,"E6"),sQuery(id+"F2.wireOp",EDGE,"E7")])]}),"instanceName":"54"});
            var Q58;
            Q58=makeQuery(id+"F4.opPattern","COPY",BODY,{"derivedFrom":makeQuery(id+"F3.opExtrude","SWEPT_BODY",BODY,{"disambiguationData":[OSD([sQuery(id+"F2.wireOp",EDGE,"E2"),sQuery(id+"F2.wireOp",EDGE,"E3"),sQuery(id+"F2.wireOp",EDGE,"E4"),sQuery(id+"F2.wireOp",EDGE,"E5"),sQuery(id+"F2.wireOp",EDGE,"E6"),sQuery(id+"F2.wireOp",EDGE,"E7")])]}),"instanceName":"55"});
            var Q59;
            Q59=makeQuery(id+"F4.opPattern","COPY",BODY,{"derivedFrom":makeQuery(id+"F3.opExtrude","SWEPT_BODY",BODY,{"disambiguationData":[OSD([sQuery(id+"F2.wireOp",EDGE,"E2"),sQuery(id+"F2.wireOp",EDGE,"E3"),sQuery(id+"F2.wireOp",EDGE,"E4"),sQuery(id+"F2.wireOp",EDGE,"E5"),sQuery(id+"F2.wireOp",EDGE,"E6"),sQuery(id+"F2.wireOp",EDGE,"E7")])]}),"instanceName":"56"});
            var Q60;
            Q60=makeQuery(id+"F4.opPattern","COPY",BODY,{"derivedFrom":makeQuery(id+"F3.opExtrude","SWEPT_BODY",BODY,{"disambiguationData":[OSD([sQuery(id+"F2.wireOp",EDGE,"E2"),sQuery(id+"F2.wireOp",EDGE,"E3"),sQuery(id+"F2.wireOp",EDGE,"E4"),sQuery(id+"F2.wireOp",EDGE,"E5"),sQuery(id+"F2.wireOp",EDGE,"E6"),sQuery(id+"F2.wireOp",EDGE,"E7")])]}),"instanceName":"57"});
            var Q61;
            Q61=makeQuery(id+"F4.opPattern","COPY",BODY,{"derivedFrom":makeQuery(id+"F3.opExtrude","SWEPT_BODY",BODY,{"disambiguationData":[OSD([sQuery(id+"F2.wireOp",EDGE,"E2"),sQuery(id+"F2.wireOp",EDGE,"E3"),sQuery(id+"F2.wireOp",EDGE,"E4"),sQuery(id+"F2.wireOp",EDGE,"E5"),sQuery(id+"F2.wireOp",EDGE,"E6"),sQuery(id+"F2.wireOp",EDGE,"E7")])]}),"instanceName":"58"});
            var Q62;
            Q62=makeQuery(id+"F4.opPattern","COPY",BODY,{"derivedFrom":makeQuery(id+"F3.opExtrude","SWEPT_BODY",BODY,{"disambiguationData":[OSD([sQuery(id+"F2.wireOp",EDGE,"E2"),sQuery(id+"F2.wireOp",EDGE,"E3"),sQuery(id+"F2.wireOp",EDGE,"E4"),sQuery(id+"F2.wireOp",EDGE,"E5"),sQuery(id+"F2.wireOp",EDGE,"E6"),sQuery(id+"F2.wireOp",EDGE,"E7")])]}),"instanceName":"59"});
            var Q63;
            Q63=makeQuery(id+"F4.opPattern","COPY",BODY,{"derivedFrom":makeQuery(id+"F3.opExtrude","SWEPT_BODY",BODY,{"disambiguationData":[OSD([sQuery(id+"F2.wireOp",EDGE,"E2"),sQuery(id+"F2.wireOp",EDGE,"E3"),sQuery(id+"F2.wireOp",EDGE,"E4"),sQuery(id+"F2.wireOp",EDGE,"E5"),sQuery(id+"F2.wireOp",EDGE,"E6"),sQuery(id+"F2.wireOp",EDGE,"E7")])]}),"instanceName":"60"});
            var Q64;
            Q64=makeQuery(id+"F4.opPattern","COPY",BODY,{"derivedFrom":makeQuery(id+"F3.opExtrude","SWEPT_BODY",BODY,{"disambiguationData":[OSD([sQuery(id+"F2.wireOp",EDGE,"E2"),sQuery(id+"F2.wireOp",EDGE,"E3"),sQuery(id+"F2.wireOp",EDGE,"E4"),sQuery(id+"F2.wireOp",EDGE,"E5"),sQuery(id+"F2.wireOp",EDGE,"E6"),sQuery(id+"F2.wireOp",EDGE,"E7")])]}),"instanceName":"61"});
            var Q65;
            Q65=makeQuery(id+"F4.opPattern","COPY",BODY,{"derivedFrom":makeQuery(id+"F3.opExtrude","SWEPT_BODY",BODY,{"disambiguationData":[OSD([sQuery(id+"F2.wireOp",EDGE,"E2"),sQuery(id+"F2.wireOp",EDGE,"E3"),sQuery(id+"F2.wireOp",EDGE,"E4"),sQuery(id+"F2.wireOp",EDGE,"E5"),sQuery(id+"F2.wireOp",EDGE,"E6"),sQuery(id+"F2.wireOp",EDGE,"E7")])]}),"instanceName":"62"});
            var Q66;
            Q66=makeQuery(id+"F4.opPattern","COPY",BODY,{"derivedFrom":makeQuery(id+"F3.opExtrude","SWEPT_BODY",BODY,{"disambiguationData":[OSD([sQuery(id+"F2.wireOp",EDGE,"E2"),sQuery(id+"F2.wireOp",EDGE,"E3"),sQuery(id+"F2.wireOp",EDGE,"E4"),sQuery(id+"F2.wireOp",EDGE,"E5"),sQuery(id+"F2.wireOp",EDGE,"E6"),sQuery(id+"F2.wireOp",EDGE,"E7")])]}),"instanceName":"63"});
            var Q67;
            Q67=makeQuery(id+"F4.opPattern","COPY",BODY,{"derivedFrom":makeQuery(id+"F3.opExtrude","SWEPT_BODY",BODY,{"disambiguationData":[OSD([sQuery(id+"F2.wireOp",EDGE,"E2"),sQuery(id+"F2.wireOp",EDGE,"E3"),sQuery(id+"F2.wireOp",EDGE,"E4"),sQuery(id+"F2.wireOp",EDGE,"E5"),sQuery(id+"F2.wireOp",EDGE,"E6"),sQuery(id+"F2.wireOp",EDGE,"E7")])]}),"instanceName":"64"});
            var Q68;
            Q68=makeQuery(id+"F4.opPattern","COPY",BODY,{"derivedFrom":makeQuery(id+"F3.opExtrude","SWEPT_BODY",BODY,{"disambiguationData":[OSD([sQuery(id+"F2.wireOp",EDGE,"E2"),sQuery(id+"F2.wireOp",EDGE,"E3"),sQuery(id+"F2.wireOp",EDGE,"E4"),sQuery(id+"F2.wireOp",EDGE,"E5"),sQuery(id+"F2.wireOp",EDGE,"E6"),sQuery(id+"F2.wireOp",EDGE,"E7")])]}),"instanceName":"65"});
            var Q69;
            Q69=makeQuery(id+"F4.opPattern","COPY",BODY,{"derivedFrom":makeQuery(id+"F3.opExtrude","SWEPT_BODY",BODY,{"disambiguationData":[OSD([sQuery(id+"F2.wireOp",EDGE,"E2"),sQuery(id+"F2.wireOp",EDGE,"E3"),sQuery(id+"F2.wireOp",EDGE,"E4"),sQuery(id+"F2.wireOp",EDGE,"E5"),sQuery(id+"F2.wireOp",EDGE,"E6"),sQuery(id+"F2.wireOp",EDGE,"E7")])]}),"instanceName":"66"});
            var Q70;
            Q70=makeQuery(id+"F4.opPattern","COPY",BODY,{"derivedFrom":makeQuery(id+"F3.opExtrude","SWEPT_BODY",BODY,{"disambiguationData":[OSD([sQuery(id+"F2.wireOp",EDGE,"E2"),sQuery(id+"F2.wireOp",EDGE,"E3"),sQuery(id+"F2.wireOp",EDGE,"E4"),sQuery(id+"F2.wireOp",EDGE,"E5"),sQuery(id+"F2.wireOp",EDGE,"E6"),sQuery(id+"F2.wireOp",EDGE,"E7")])]}),"instanceName":"67"});
            var Q71;
            Q71=makeQuery(id+"F4.opPattern","COPY",BODY,{"derivedFrom":makeQuery(id+"F3.opExtrude","SWEPT_BODY",BODY,{"disambiguationData":[OSD([sQuery(id+"F2.wireOp",EDGE,"E2"),sQuery(id+"F2.wireOp",EDGE,"E3"),sQuery(id+"F2.wireOp",EDGE,"E4"),sQuery(id+"F2.wireOp",EDGE,"E5"),sQuery(id+"F2.wireOp",EDGE,"E6"),sQuery(id+"F2.wireOp",EDGE,"E7")])]}),"instanceName":"68"});
            var Q72;
            Q72=makeQuery(id+"F4.opPattern","COPY",BODY,{"derivedFrom":makeQuery(id+"F3.opExtrude","SWEPT_BODY",BODY,{"disambiguationData":[OSD([sQuery(id+"F2.wireOp",EDGE,"E2"),sQuery(id+"F2.wireOp",EDGE,"E3"),sQuery(id+"F2.wireOp",EDGE,"E4"),sQuery(id+"F2.wireOp",EDGE,"E5"),sQuery(id+"F2.wireOp",EDGE,"E6"),sQuery(id+"F2.wireOp",EDGE,"E7")])]}),"instanceName":"69"});
            var Q73;
            Q73=makeQuery(id+"F4.opPattern","COPY",BODY,{"derivedFrom":makeQuery(id+"F3.opExtrude","SWEPT_BODY",BODY,{"disambiguationData":[OSD([sQuery(id+"F2.wireOp",EDGE,"E2"),sQuery(id+"F2.wireOp",EDGE,"E3"),sQuery(id+"F2.wireOp",EDGE,"E4"),sQuery(id+"F2.wireOp",EDGE,"E5"),sQuery(id+"F2.wireOp",EDGE,"E6"),sQuery(id+"F2.wireOp",EDGE,"E7")])]}),"instanceName":"70"});
            var Q74;
            Q74=makeQuery(id+"F4.opPattern","COPY",BODY,{"derivedFrom":makeQuery(id+"F3.opExtrude","SWEPT_BODY",BODY,{"disambiguationData":[OSD([sQuery(id+"F2.wireOp",EDGE,"E2"),sQuery(id+"F2.wireOp",EDGE,"E3"),sQuery(id+"F2.wireOp",EDGE,"E4"),sQuery(id+"F2.wireOp",EDGE,"E5"),sQuery(id+"F2.wireOp",EDGE,"E6"),sQuery(id+"F2.wireOp",EDGE,"E7")])]}),"instanceName":"71"});
            var Q75;
            Q75=makeQuery(id+"F4.opPattern","COPY",BODY,{"derivedFrom":makeQuery(id+"F3.opExtrude","SWEPT_BODY",BODY,{"disambiguationData":[OSD([sQuery(id+"F2.wireOp",EDGE,"E2"),sQuery(id+"F2.wireOp",EDGE,"E3"),sQuery(id+"F2.wireOp",EDGE,"E4"),sQuery(id+"F2.wireOp",EDGE,"E5"),sQuery(id+"F2.wireOp",EDGE,"E6"),sQuery(id+"F2.wireOp",EDGE,"E7")])]}),"instanceName":"72"});
            var Q76;
            Q76=makeQuery(id+"F4.opPattern","COPY",BODY,{"derivedFrom":makeQuery(id+"F3.opExtrude","SWEPT_BODY",BODY,{"disambiguationData":[OSD([sQuery(id+"F2.wireOp",EDGE,"E2"),sQuery(id+"F2.wireOp",EDGE,"E3"),sQuery(id+"F2.wireOp",EDGE,"E4"),sQuery(id+"F2.wireOp",EDGE,"E5"),sQuery(id+"F2.wireOp",EDGE,"E6"),sQuery(id+"F2.wireOp",EDGE,"E7")])]}),"instanceName":"73"});
            var Q77;
            Q77=makeQuery(id+"F4.opPattern","COPY",BODY,{"derivedFrom":makeQuery(id+"F3.opExtrude","SWEPT_BODY",BODY,{"disambiguationData":[OSD([sQuery(id+"F2.wireOp",EDGE,"E2"),sQuery(id+"F2.wireOp",EDGE,"E3"),sQuery(id+"F2.wireOp",EDGE,"E4"),sQuery(id+"F2.wireOp",EDGE,"E5"),sQuery(id+"F2.wireOp",EDGE,"E6"),sQuery(id+"F2.wireOp",EDGE,"E7")])]}),"instanceName":"74"});
            var Q78;
            Q78=makeQuery(id+"F4.opPattern","COPY",BODY,{"derivedFrom":makeQuery(id+"F3.opExtrude","SWEPT_BODY",BODY,{"disambiguationData":[OSD([sQuery(id+"F2.wireOp",EDGE,"E2"),sQuery(id+"F2.wireOp",EDGE,"E3"),sQuery(id+"F2.wireOp",EDGE,"E4"),sQuery(id+"F2.wireOp",EDGE,"E5"),sQuery(id+"F2.wireOp",EDGE,"E6"),sQuery(id+"F2.wireOp",EDGE,"E7")])]}),"instanceName":"75"});
            var Q79;
            Q79=makeQuery(id+"F4.opPattern","COPY",BODY,{"derivedFrom":makeQuery(id+"F3.opExtrude","SWEPT_BODY",BODY,{"disambiguationData":[OSD([sQuery(id+"F2.wireOp",EDGE,"E2"),sQuery(id+"F2.wireOp",EDGE,"E3"),sQuery(id+"F2.wireOp",EDGE,"E4"),sQuery(id+"F2.wireOp",EDGE,"E5"),sQuery(id+"F2.wireOp",EDGE,"E6"),sQuery(id+"F2.wireOp",EDGE,"E7")])]}),"instanceName":"76"});
            var Q80;
            Q80=makeQuery(id+"F4.opPattern","COPY",BODY,{"derivedFrom":makeQuery(id+"F3.opExtrude","SWEPT_BODY",BODY,{"disambiguationData":[OSD([sQuery(id+"F2.wireOp",EDGE,"E2"),sQuery(id+"F2.wireOp",EDGE,"E3"),sQuery(id+"F2.wireOp",EDGE,"E4"),sQuery(id+"F2.wireOp",EDGE,"E5"),sQuery(id+"F2.wireOp",EDGE,"E6"),sQuery(id+"F2.wireOp",EDGE,"E7")])]}),"instanceName":"77"});
            var Q81;
            Q81=makeQuery(id+"F4.opPattern","COPY",BODY,{"derivedFrom":makeQuery(id+"F3.opExtrude","SWEPT_BODY",BODY,{"disambiguationData":[OSD([sQuery(id+"F2.wireOp",EDGE,"E2"),sQuery(id+"F2.wireOp",EDGE,"E3"),sQuery(id+"F2.wireOp",EDGE,"E4"),sQuery(id+"F2.wireOp",EDGE,"E5"),sQuery(id+"F2.wireOp",EDGE,"E6"),sQuery(id+"F2.wireOp",EDGE,"E7")])]}),"instanceName":"78"});
            var Q82;
            Q82=makeQuery(id+"F4.opPattern","COPY",BODY,{"derivedFrom":makeQuery(id+"F3.opExtrude","SWEPT_BODY",BODY,{"disambiguationData":[OSD([sQuery(id+"F2.wireOp",EDGE,"E2"),sQuery(id+"F2.wireOp",EDGE,"E3"),sQuery(id+"F2.wireOp",EDGE,"E4"),sQuery(id+"F2.wireOp",EDGE,"E5"),sQuery(id+"F2.wireOp",EDGE,"E6"),sQuery(id+"F2.wireOp",EDGE,"E7")])]}),"instanceName":"79"});
            var Q83;
            Q83=makeQuery(id+"F4.opPattern","COPY",BODY,{"derivedFrom":makeQuery(id+"F3.opExtrude","SWEPT_BODY",BODY,{"disambiguationData":[OSD([sQuery(id+"F2.wireOp",EDGE,"E2"),sQuery(id+"F2.wireOp",EDGE,"E3"),sQuery(id+"F2.wireOp",EDGE,"E4"),sQuery(id+"F2.wireOp",EDGE,"E5"),sQuery(id+"F2.wireOp",EDGE,"E6"),sQuery(id+"F2.wireOp",EDGE,"E7")])]}),"instanceName":"80"});
            var Q84;
            Q84=makeQuery(id+"F4.opPattern","COPY",BODY,{"derivedFrom":makeQuery(id+"F3.opExtrude","SWEPT_BODY",BODY,{"disambiguationData":[OSD([sQuery(id+"F2.wireOp",EDGE,"E2"),sQuery(id+"F2.wireOp",EDGE,"E3"),sQuery(id+"F2.wireOp",EDGE,"E4"),sQuery(id+"F2.wireOp",EDGE,"E5"),sQuery(id+"F2.wireOp",EDGE,"E6"),sQuery(id+"F2.wireOp",EDGE,"E7")])]}),"instanceName":"81"});
            var Q85;
            Q85=makeQuery(id+"F4.opPattern","COPY",BODY,{"derivedFrom":makeQuery(id+"F3.opExtrude","SWEPT_BODY",BODY,{"disambiguationData":[OSD([sQuery(id+"F2.wireOp",EDGE,"E2"),sQuery(id+"F2.wireOp",EDGE,"E3"),sQuery(id+"F2.wireOp",EDGE,"E4"),sQuery(id+"F2.wireOp",EDGE,"E5"),sQuery(id+"F2.wireOp",EDGE,"E6"),sQuery(id+"F2.wireOp",EDGE,"E7")])]}),"instanceName":"82"});
            var Q86;
            Q86=makeQuery(id+"F4.opPattern","COPY",BODY,{"derivedFrom":makeQuery(id+"F3.opExtrude","SWEPT_BODY",BODY,{"disambiguationData":[OSD([sQuery(id+"F2.wireOp",EDGE,"E2"),sQuery(id+"F2.wireOp",EDGE,"E3"),sQuery(id+"F2.wireOp",EDGE,"E4"),sQuery(id+"F2.wireOp",EDGE,"E5"),sQuery(id+"F2.wireOp",EDGE,"E6"),sQuery(id+"F2.wireOp",EDGE,"E7")])]}),"instanceName":"83"});
            var Q87;
            Q87=makeQuery(id+"F4.opPattern","COPY",BODY,{"derivedFrom":makeQuery(id+"F3.opExtrude","SWEPT_BODY",BODY,{"disambiguationData":[OSD([sQuery(id+"F2.wireOp",EDGE,"E2"),sQuery(id+"F2.wireOp",EDGE,"E3"),sQuery(id+"F2.wireOp",EDGE,"E4"),sQuery(id+"F2.wireOp",EDGE,"E5"),sQuery(id+"F2.wireOp",EDGE,"E6"),sQuery(id+"F2.wireOp",EDGE,"E7")])]}),"instanceName":"84"});
            var Q88;
            Q88=makeQuery(id+"F4.opPattern","COPY",BODY,{"derivedFrom":makeQuery(id+"F3.opExtrude","SWEPT_BODY",BODY,{"disambiguationData":[OSD([sQuery(id+"F2.wireOp",EDGE,"E2"),sQuery(id+"F2.wireOp",EDGE,"E3"),sQuery(id+"F2.wireOp",EDGE,"E4"),sQuery(id+"F2.wireOp",EDGE,"E5"),sQuery(id+"F2.wireOp",EDGE,"E6"),sQuery(id+"F2.wireOp",EDGE,"E7")])]}),"instanceName":"85"});
            var Q89;
            Q89=makeQuery(id+"F4.opPattern","COPY",BODY,{"derivedFrom":makeQuery(id+"F3.opExtrude","SWEPT_BODY",BODY,{"disambiguationData":[OSD([sQuery(id+"F2.wireOp",EDGE,"E2"),sQuery(id+"F2.wireOp",EDGE,"E3"),sQuery(id+"F2.wireOp",EDGE,"E4"),sQuery(id+"F2.wireOp",EDGE,"E5"),sQuery(id+"F2.wireOp",EDGE,"E6"),sQuery(id+"F2.wireOp",EDGE,"E7")])]}),"instanceName":"86"});
            var Q90;
            Q90=makeQuery(id+"F4.opPattern","COPY",BODY,{"derivedFrom":makeQuery(id+"F3.opExtrude","SWEPT_BODY",BODY,{"disambiguationData":[OSD([sQuery(id+"F2.wireOp",EDGE,"E2"),sQuery(id+"F2.wireOp",EDGE,"E3"),sQuery(id+"F2.wireOp",EDGE,"E4"),sQuery(id+"F2.wireOp",EDGE,"E5"),sQuery(id+"F2.wireOp",EDGE,"E6"),sQuery(id+"F2.wireOp",EDGE,"E7")])]}),"instanceName":"87"});
            var Q91;
            Q91=makeQuery(id+"F4.opPattern","COPY",BODY,{"derivedFrom":makeQuery(id+"F3.opExtrude","SWEPT_BODY",BODY,{"disambiguationData":[OSD([sQuery(id+"F2.wireOp",EDGE,"E2"),sQuery(id+"F2.wireOp",EDGE,"E3"),sQuery(id+"F2.wireOp",EDGE,"E4"),sQuery(id+"F2.wireOp",EDGE,"E5"),sQuery(id+"F2.wireOp",EDGE,"E6"),sQuery(id+"F2.wireOp",EDGE,"E7")])]}),"instanceName":"88"});
            var Q92;
            Q92=makeQuery(id+"F4.opPattern","COPY",BODY,{"derivedFrom":makeQuery(id+"F3.opExtrude","SWEPT_BODY",BODY,{"disambiguationData":[OSD([sQuery(id+"F2.wireOp",EDGE,"E2"),sQuery(id+"F2.wireOp",EDGE,"E3"),sQuery(id+"F2.wireOp",EDGE,"E4"),sQuery(id+"F2.wireOp",EDGE,"E5"),sQuery(id+"F2.wireOp",EDGE,"E6"),sQuery(id+"F2.wireOp",EDGE,"E7")])]}),"instanceName":"89"});
            var Q93;
            Q93=makeQuery(id+"F4.opPattern","COPY",BODY,{"derivedFrom":makeQuery(id+"F3.opExtrude","SWEPT_BODY",BODY,{"disambiguationData":[OSD([sQuery(id+"F2.wireOp",EDGE,"E2"),sQuery(id+"F2.wireOp",EDGE,"E3"),sQuery(id+"F2.wireOp",EDGE,"E4"),sQuery(id+"F2.wireOp",EDGE,"E5"),sQuery(id+"F2.wireOp",EDGE,"E6"),sQuery(id+"F2.wireOp",EDGE,"E7")])]}),"instanceName":"90"});
            var Q94;
            Q94=makeQuery(id+"F4.opPattern","COPY",BODY,{"derivedFrom":makeQuery(id+"F3.opExtrude","SWEPT_BODY",BODY,{"disambiguationData":[OSD([sQuery(id+"F2.wireOp",EDGE,"E2"),sQuery(id+"F2.wireOp",EDGE,"E3"),sQuery(id+"F2.wireOp",EDGE,"E4"),sQuery(id+"F2.wireOp",EDGE,"E5"),sQuery(id+"F2.wireOp",EDGE,"E6"),sQuery(id+"F2.wireOp",EDGE,"E7")])]}),"instanceName":"91"});
            var Q95;
            Q95=makeQuery(id+"F4.opPattern","COPY",BODY,{"derivedFrom":makeQuery(id+"F3.opExtrude","SWEPT_BODY",BODY,{"disambiguationData":[OSD([sQuery(id+"F2.wireOp",EDGE,"E2"),sQuery(id+"F2.wireOp",EDGE,"E3"),sQuery(id+"F2.wireOp",EDGE,"E4"),sQuery(id+"F2.wireOp",EDGE,"E5"),sQuery(id+"F2.wireOp",EDGE,"E6"),sQuery(id+"F2.wireOp",EDGE,"E7")])]}),"instanceName":"92"});
            var Q96;
            Q96=makeQuery(id+"F4.opPattern","COPY",BODY,{"derivedFrom":makeQuery(id+"F3.opExtrude","SWEPT_BODY",BODY,{"disambiguationData":[OSD([sQuery(id+"F2.wireOp",EDGE,"E2"),sQuery(id+"F2.wireOp",EDGE,"E3"),sQuery(id+"F2.wireOp",EDGE,"E4"),sQuery(id+"F2.wireOp",EDGE,"E5"),sQuery(id+"F2.wireOp",EDGE,"E6"),sQuery(id+"F2.wireOp",EDGE,"E7")])]}),"instanceName":"93"});
            var Q97;
            Q97=makeQuery(id+"F4.opPattern","COPY",BODY,{"derivedFrom":makeQuery(id+"F3.opExtrude","SWEPT_BODY",BODY,{"disambiguationData":[OSD([sQuery(id+"F2.wireOp",EDGE,"E2"),sQuery(id+"F2.wireOp",EDGE,"E3"),sQuery(id+"F2.wireOp",EDGE,"E4"),sQuery(id+"F2.wireOp",EDGE,"E5"),sQuery(id+"F2.wireOp",EDGE,"E6"),sQuery(id+"F2.wireOp",EDGE,"E7")])]}),"instanceName":"94"});
            var Q98;
            Q98=makeQuery(id+"F4.opPattern","COPY",BODY,{"derivedFrom":makeQuery(id+"F3.opExtrude","SWEPT_BODY",BODY,{"disambiguationData":[OSD([sQuery(id+"F2.wireOp",EDGE,"E2"),sQuery(id+"F2.wireOp",EDGE,"E3"),sQuery(id+"F2.wireOp",EDGE,"E4"),sQuery(id+"F2.wireOp",EDGE,"E5"),sQuery(id+"F2.wireOp",EDGE,"E6"),sQuery(id+"F2.wireOp",EDGE,"E7")])]}),"instanceName":"95"});
            var Q99;
            Q99=makeQuery(id+"F4.opPattern","COPY",BODY,{"derivedFrom":makeQuery(id+"F3.opExtrude","SWEPT_BODY",BODY,{"disambiguationData":[OSD([sQuery(id+"F2.wireOp",EDGE,"E2"),sQuery(id+"F2.wireOp",EDGE,"E3"),sQuery(id+"F2.wireOp",EDGE,"E4"),sQuery(id+"F2.wireOp",EDGE,"E5"),sQuery(id+"F2.wireOp",EDGE,"E6"),sQuery(id+"F2.wireOp",EDGE,"E7")])]}),"instanceName":"96"});
            var Q100;
            Q100=makeQuery(id+"F4.opPattern","COPY",BODY,{"derivedFrom":makeQuery(id+"F3.opExtrude","SWEPT_BODY",BODY,{"disambiguationData":[OSD([sQuery(id+"F2.wireOp",EDGE,"E2"),sQuery(id+"F2.wireOp",EDGE,"E3"),sQuery(id+"F2.wireOp",EDGE,"E4"),sQuery(id+"F2.wireOp",EDGE,"E5"),sQuery(id+"F2.wireOp",EDGE,"E6"),sQuery(id+"F2.wireOp",EDGE,"E7")])]}),"instanceName":"97"});
            var Q101;
            Q101=makeQuery(id+"F4.opPattern","COPY",BODY,{"derivedFrom":makeQuery(id+"F3.opExtrude","SWEPT_BODY",BODY,{"disambiguationData":[OSD([sQuery(id+"F2.wireOp",EDGE,"E2"),sQuery(id+"F2.wireOp",EDGE,"E3"),sQuery(id+"F2.wireOp",EDGE,"E4"),sQuery(id+"F2.wireOp",EDGE,"E5"),sQuery(id+"F2.wireOp",EDGE,"E6"),sQuery(id+"F2.wireOp",EDGE,"E7")])]}),"instanceName":"98"});
            var Q102;
            Q102=makeQuery(id+"F4.opPattern","COPY",BODY,{"derivedFrom":makeQuery(id+"F3.opExtrude","SWEPT_BODY",BODY,{"disambiguationData":[OSD([sQuery(id+"F2.wireOp",EDGE,"E2"),sQuery(id+"F2.wireOp",EDGE,"E3"),sQuery(id+"F2.wireOp",EDGE,"E4"),sQuery(id+"F2.wireOp",EDGE,"E5"),sQuery(id+"F2.wireOp",EDGE,"E6"),sQuery(id+"F2.wireOp",EDGE,"E7")])]}),"instanceName":"99"});
            var Q103;
            Q103=makeQuery(id+"F4.opPattern","COPY",BODY,{"derivedFrom":makeQuery(id+"F3.opExtrude","SWEPT_BODY",BODY,{"disambiguationData":[OSD([sQuery(id+"F2.wireOp",EDGE,"E2"),sQuery(id+"F2.wireOp",EDGE,"E3"),sQuery(id+"F2.wireOp",EDGE,"E4"),sQuery(id+"F2.wireOp",EDGE,"E5"),sQuery(id+"F2.wireOp",EDGE,"E6"),sQuery(id+"F2.wireOp",EDGE,"E7")])]}),"instanceName":"100"});
            var Q104;
            Q104=makeQuery(id+"F4.opPattern","COPY",BODY,{"derivedFrom":makeQuery(id+"F3.opExtrude","SWEPT_BODY",BODY,{"disambiguationData":[OSD([sQuery(id+"F2.wireOp",EDGE,"E2"),sQuery(id+"F2.wireOp",EDGE,"E3"),sQuery(id+"F2.wireOp",EDGE,"E4"),sQuery(id+"F2.wireOp",EDGE,"E5"),sQuery(id+"F2.wireOp",EDGE,"E6"),sQuery(id+"F2.wireOp",EDGE,"E7")])]}),"instanceName":"101"});
            var Q105;
            Q105=makeQuery(id+"F4.opPattern","COPY",BODY,{"derivedFrom":makeQuery(id+"F3.opExtrude","SWEPT_BODY",BODY,{"disambiguationData":[OSD([sQuery(id+"F2.wireOp",EDGE,"E2"),sQuery(id+"F2.wireOp",EDGE,"E3"),sQuery(id+"F2.wireOp",EDGE,"E4"),sQuery(id+"F2.wireOp",EDGE,"E5"),sQuery(id+"F2.wireOp",EDGE,"E6"),sQuery(id+"F2.wireOp",EDGE,"E7")])]}),"instanceName":"102"});
            var Q106;
            Q106=makeQuery(id+"F4.opPattern","COPY",BODY,{"derivedFrom":makeQuery(id+"F3.opExtrude","SWEPT_BODY",BODY,{"disambiguationData":[OSD([sQuery(id+"F2.wireOp",EDGE,"E2"),sQuery(id+"F2.wireOp",EDGE,"E3"),sQuery(id+"F2.wireOp",EDGE,"E4"),sQuery(id+"F2.wireOp",EDGE,"E5"),sQuery(id+"F2.wireOp",EDGE,"E6"),sQuery(id+"F2.wireOp",EDGE,"E7")])]}),"instanceName":"103"});
            var Q107;
            Q107=makeQuery(id+"F4.opPattern","COPY",BODY,{"derivedFrom":makeQuery(id+"F3.opExtrude","SWEPT_BODY",BODY,{"disambiguationData":[OSD([sQuery(id+"F2.wireOp",EDGE,"E2"),sQuery(id+"F2.wireOp",EDGE,"E3"),sQuery(id+"F2.wireOp",EDGE,"E4"),sQuery(id+"F2.wireOp",EDGE,"E5"),sQuery(id+"F2.wireOp",EDGE,"E6"),sQuery(id+"F2.wireOp",EDGE,"E7")])]}),"instanceName":"104"});
            var Q108;
            Q108=makeQuery(id+"F4.opPattern","COPY",BODY,{"derivedFrom":makeQuery(id+"F3.opExtrude","SWEPT_BODY",BODY,{"disambiguationData":[OSD([sQuery(id+"F2.wireOp",EDGE,"E2"),sQuery(id+"F2.wireOp",EDGE,"E3"),sQuery(id+"F2.wireOp",EDGE,"E4"),sQuery(id+"F2.wireOp",EDGE,"E5"),sQuery(id+"F2.wireOp",EDGE,"E6"),sQuery(id+"F2.wireOp",EDGE,"E7")])]}),"instanceName":"105"});
            var Q109;
            Q109=makeQuery(id+"F4.opPattern","COPY",BODY,{"derivedFrom":makeQuery(id+"F3.opExtrude","SWEPT_BODY",BODY,{"disambiguationData":[OSD([sQuery(id+"F2.wireOp",EDGE,"E2"),sQuery(id+"F2.wireOp",EDGE,"E3"),sQuery(id+"F2.wireOp",EDGE,"E4"),sQuery(id+"F2.wireOp",EDGE,"E5"),sQuery(id+"F2.wireOp",EDGE,"E6"),sQuery(id+"F2.wireOp",EDGE,"E7")])]}),"instanceName":"106"});
            var Q110;
            Q110=makeQuery(id+"F4.opPattern","COPY",BODY,{"derivedFrom":makeQuery(id+"F3.opExtrude","SWEPT_BODY",BODY,{"disambiguationData":[OSD([sQuery(id+"F2.wireOp",EDGE,"E2"),sQuery(id+"F2.wireOp",EDGE,"E3"),sQuery(id+"F2.wireOp",EDGE,"E4"),sQuery(id+"F2.wireOp",EDGE,"E5"),sQuery(id+"F2.wireOp",EDGE,"E6"),sQuery(id+"F2.wireOp",EDGE,"E7")])]}),"instanceName":"107"});
            var Q111;
            Q111=makeQuery(id+"F4.opPattern","COPY",BODY,{"derivedFrom":makeQuery(id+"F3.opExtrude","SWEPT_BODY",BODY,{"disambiguationData":[OSD([sQuery(id+"F2.wireOp",EDGE,"E2"),sQuery(id+"F2.wireOp",EDGE,"E3"),sQuery(id+"F2.wireOp",EDGE,"E4"),sQuery(id+"F2.wireOp",EDGE,"E5"),sQuery(id+"F2.wireOp",EDGE,"E6"),sQuery(id+"F2.wireOp",EDGE,"E7")])]}),"instanceName":"108"});
            var Q112;
            Q112=makeQuery(id+"F4.opPattern","COPY",BODY,{"derivedFrom":makeQuery(id+"F3.opExtrude","SWEPT_BODY",BODY,{"disambiguationData":[OSD([sQuery(id+"F2.wireOp",EDGE,"E2"),sQuery(id+"F2.wireOp",EDGE,"E3"),sQuery(id+"F2.wireOp",EDGE,"E4"),sQuery(id+"F2.wireOp",EDGE,"E5"),sQuery(id+"F2.wireOp",EDGE,"E6"),sQuery(id+"F2.wireOp",EDGE,"E7")])]}),"instanceName":"109"});
            var Q113;
            Q113=makeQuery(id+"F4.opPattern","COPY",BODY,{"derivedFrom":makeQuery(id+"F3.opExtrude","SWEPT_BODY",BODY,{"disambiguationData":[OSD([sQuery(id+"F2.wireOp",EDGE,"E2"),sQuery(id+"F2.wireOp",EDGE,"E3"),sQuery(id+"F2.wireOp",EDGE,"E4"),sQuery(id+"F2.wireOp",EDGE,"E5"),sQuery(id+"F2.wireOp",EDGE,"E6"),sQuery(id+"F2.wireOp",EDGE,"E7")])]}),"instanceName":"110"});
            var Q114;
            Q114=makeQuery(id+"F4.opPattern","COPY",BODY,{"derivedFrom":makeQuery(id+"F3.opExtrude","SWEPT_BODY",BODY,{"disambiguationData":[OSD([sQuery(id+"F2.wireOp",EDGE,"E2"),sQuery(id+"F2.wireOp",EDGE,"E3"),sQuery(id+"F2.wireOp",EDGE,"E4"),sQuery(id+"F2.wireOp",EDGE,"E5"),sQuery(id+"F2.wireOp",EDGE,"E6"),sQuery(id+"F2.wireOp",EDGE,"E7")])]}),"instanceName":"111"});
            var Q115;
            Q115=makeQuery(id+"F4.opPattern","COPY",BODY,{"derivedFrom":makeQuery(id+"F3.opExtrude","SWEPT_BODY",BODY,{"disambiguationData":[OSD([sQuery(id+"F2.wireOp",EDGE,"E2"),sQuery(id+"F2.wireOp",EDGE,"E3"),sQuery(id+"F2.wireOp",EDGE,"E4"),sQuery(id+"F2.wireOp",EDGE,"E5"),sQuery(id+"F2.wireOp",EDGE,"E6"),sQuery(id+"F2.wireOp",EDGE,"E7")])]}),"instanceName":"112"});
            var Q116;
            Q116=makeQuery(id+"F4.opPattern","COPY",BODY,{"derivedFrom":makeQuery(id+"F3.opExtrude","SWEPT_BODY",BODY,{"disambiguationData":[OSD([sQuery(id+"F2.wireOp",EDGE,"E2"),sQuery(id+"F2.wireOp",EDGE,"E3"),sQuery(id+"F2.wireOp",EDGE,"E4"),sQuery(id+"F2.wireOp",EDGE,"E5"),sQuery(id+"F2.wireOp",EDGE,"E6"),sQuery(id+"F2.wireOp",EDGE,"E7")])]}),"instanceName":"113"});
            var Q117;
            Q117=makeQuery(id+"F4.opPattern","COPY",BODY,{"derivedFrom":makeQuery(id+"F3.opExtrude","SWEPT_BODY",BODY,{"disambiguationData":[OSD([sQuery(id+"F2.wireOp",EDGE,"E2"),sQuery(id+"F2.wireOp",EDGE,"E3"),sQuery(id+"F2.wireOp",EDGE,"E4"),sQuery(id+"F2.wireOp",EDGE,"E5"),sQuery(id+"F2.wireOp",EDGE,"E6"),sQuery(id+"F2.wireOp",EDGE,"E7")])]}),"instanceName":"114"});
            var Q118;
            Q118=makeQuery(id+"F4.opPattern","COPY",BODY,{"derivedFrom":makeQuery(id+"F3.opExtrude","SWEPT_BODY",BODY,{"disambiguationData":[OSD([sQuery(id+"F2.wireOp",EDGE,"E2"),sQuery(id+"F2.wireOp",EDGE,"E3"),sQuery(id+"F2.wireOp",EDGE,"E4"),sQuery(id+"F2.wireOp",EDGE,"E5"),sQuery(id+"F2.wireOp",EDGE,"E6"),sQuery(id+"F2.wireOp",EDGE,"E7")])]}),"instanceName":"115"});
            var Q119;
            Q119=makeQuery(id+"F4.opPattern","COPY",BODY,{"derivedFrom":makeQuery(id+"F3.opExtrude","SWEPT_BODY",BODY,{"disambiguationData":[OSD([sQuery(id+"F2.wireOp",EDGE,"E2"),sQuery(id+"F2.wireOp",EDGE,"E3"),sQuery(id+"F2.wireOp",EDGE,"E4"),sQuery(id+"F2.wireOp",EDGE,"E5"),sQuery(id+"F2.wireOp",EDGE,"E6"),sQuery(id+"F2.wireOp",EDGE,"E7")])]}),"instanceName":"116"});
            var Q120;
            Q120=makeQuery(id+"F4.opPattern","COPY",BODY,{"derivedFrom":makeQuery(id+"F3.opExtrude","SWEPT_BODY",BODY,{"disambiguationData":[OSD([sQuery(id+"F2.wireOp",EDGE,"E2"),sQuery(id+"F2.wireOp",EDGE,"E3"),sQuery(id+"F2.wireOp",EDGE,"E4"),sQuery(id+"F2.wireOp",EDGE,"E5"),sQuery(id+"F2.wireOp",EDGE,"E6"),sQuery(id+"F2.wireOp",EDGE,"E7")])]}),"instanceName":"117"});
            var Q121;
            Q121=makeQuery(id+"F4.opPattern","COPY",BODY,{"derivedFrom":makeQuery(id+"F3.opExtrude","SWEPT_BODY",BODY,{"disambiguationData":[OSD([sQuery(id+"F2.wireOp",EDGE,"E2"),sQuery(id+"F2.wireOp",EDGE,"E3"),sQuery(id+"F2.wireOp",EDGE,"E4"),sQuery(id+"F2.wireOp",EDGE,"E5"),sQuery(id+"F2.wireOp",EDGE,"E6"),sQuery(id+"F2.wireOp",EDGE,"E7")])]}),"instanceName":"118"});
            var Q122;
            Q122=makeQuery(id+"F4.opPattern","COPY",BODY,{"derivedFrom":makeQuery(id+"F3.opExtrude","SWEPT_BODY",BODY,{"disambiguationData":[OSD([sQuery(id+"F2.wireOp",EDGE,"E2"),sQuery(id+"F2.wireOp",EDGE,"E3"),sQuery(id+"F2.wireOp",EDGE,"E4"),sQuery(id+"F2.wireOp",EDGE,"E5"),sQuery(id+"F2.wireOp",EDGE,"E6"),sQuery(id+"F2.wireOp",EDGE,"E7")])]}),"instanceName":"119"});
            var Q123;
            Q123=makeQuery(id+"F4.opPattern","COPY",BODY,{"derivedFrom":makeQuery(id+"F3.opExtrude","SWEPT_BODY",BODY,{"disambiguationData":[OSD([sQuery(id+"F2.wireOp",EDGE,"E2"),sQuery(id+"F2.wireOp",EDGE,"E3"),sQuery(id+"F2.wireOp",EDGE,"E4"),sQuery(id+"F2.wireOp",EDGE,"E5"),sQuery(id+"F2.wireOp",EDGE,"E6"),sQuery(id+"F2.wireOp",EDGE,"E7")])]}),"instanceName":"120"});
            var Q124;
            Q124=makeQuery(id+"F4.opPattern","COPY",BODY,{"derivedFrom":makeQuery(id+"F3.opExtrude","SWEPT_BODY",BODY,{"disambiguationData":[OSD([sQuery(id+"F2.wireOp",EDGE,"E2"),sQuery(id+"F2.wireOp",EDGE,"E3"),sQuery(id+"F2.wireOp",EDGE,"E4"),sQuery(id+"F2.wireOp",EDGE,"E5"),sQuery(id+"F2.wireOp",EDGE,"E6"),sQuery(id+"F2.wireOp",EDGE,"E7")])]}),"instanceName":"121"});
            var Q125;
            Q125=makeQuery(id+"F4.opPattern","COPY",BODY,{"derivedFrom":makeQuery(id+"F3.opExtrude","SWEPT_BODY",BODY,{"disambiguationData":[OSD([sQuery(id+"F2.wireOp",EDGE,"E2"),sQuery(id+"F2.wireOp",EDGE,"E3"),sQuery(id+"F2.wireOp",EDGE,"E4"),sQuery(id+"F2.wireOp",EDGE,"E5"),sQuery(id+"F2.wireOp",EDGE,"E6"),sQuery(id+"F2.wireOp",EDGE,"E7")])]}),"instanceName":"122"});
            var Q126;
            Q126=makeQuery(id+"F4.opPattern","COPY",BODY,{"derivedFrom":makeQuery(id+"F3.opExtrude","SWEPT_BODY",BODY,{"disambiguationData":[OSD([sQuery(id+"F2.wireOp",EDGE,"E2"),sQuery(id+"F2.wireOp",EDGE,"E3"),sQuery(id+"F2.wireOp",EDGE,"E4"),sQuery(id+"F2.wireOp",EDGE,"E5"),sQuery(id+"F2.wireOp",EDGE,"E6"),sQuery(id+"F2.wireOp",EDGE,"E7")])]}),"instanceName":"123"});
            var Q127;
            Q127=makeQuery(id+"F4.opPattern","COPY",BODY,{"derivedFrom":makeQuery(id+"F3.opExtrude","SWEPT_BODY",BODY,{"disambiguationData":[OSD([sQuery(id+"F2.wireOp",EDGE,"E2"),sQuery(id+"F2.wireOp",EDGE,"E3"),sQuery(id+"F2.wireOp",EDGE,"E4"),sQuery(id+"F2.wireOp",EDGE,"E5"),sQuery(id+"F2.wireOp",EDGE,"E6"),sQuery(id+"F2.wireOp",EDGE,"E7")])]}),"instanceName":"124"});
            var Q128;
            Q128=makeQuery(id+"F4.opPattern","COPY",BODY,{"derivedFrom":makeQuery(id+"F3.opExtrude","SWEPT_BODY",BODY,{"disambiguationData":[OSD([sQuery(id+"F2.wireOp",EDGE,"E2"),sQuery(id+"F2.wireOp",EDGE,"E3"),sQuery(id+"F2.wireOp",EDGE,"E4"),sQuery(id+"F2.wireOp",EDGE,"E5"),sQuery(id+"F2.wireOp",EDGE,"E6"),sQuery(id+"F2.wireOp",EDGE,"E7")])]}),"instanceName":"125"});
            var Q129;
            Q129=makeQuery(id+"F4.opPattern","COPY",BODY,{"derivedFrom":makeQuery(id+"F3.opExtrude","SWEPT_BODY",BODY,{"disambiguationData":[OSD([sQuery(id+"F2.wireOp",EDGE,"E2"),sQuery(id+"F2.wireOp",EDGE,"E3"),sQuery(id+"F2.wireOp",EDGE,"E4"),sQuery(id+"F2.wireOp",EDGE,"E5"),sQuery(id+"F2.wireOp",EDGE,"E6"),sQuery(id+"F2.wireOp",EDGE,"E7")])]}),"instanceName":"126"});
            var Q130;
            Q130=makeQuery(id+"F4.opPattern","COPY",BODY,{"derivedFrom":makeQuery(id+"F3.opExtrude","SWEPT_BODY",BODY,{"disambiguationData":[OSD([sQuery(id+"F2.wireOp",EDGE,"E2"),sQuery(id+"F2.wireOp",EDGE,"E3"),sQuery(id+"F2.wireOp",EDGE,"E4"),sQuery(id+"F2.wireOp",EDGE,"E5"),sQuery(id+"F2.wireOp",EDGE,"E6"),sQuery(id+"F2.wireOp",EDGE,"E7")])]}),"instanceName":"127"});
            var Q131;
            Q131=makeQuery(id+"F4.opPattern","COPY",BODY,{"derivedFrom":makeQuery(id+"F3.opExtrude","SWEPT_BODY",BODY,{"disambiguationData":[OSD([sQuery(id+"F2.wireOp",EDGE,"E2"),sQuery(id+"F2.wireOp",EDGE,"E3"),sQuery(id+"F2.wireOp",EDGE,"E4"),sQuery(id+"F2.wireOp",EDGE,"E5"),sQuery(id+"F2.wireOp",EDGE,"E6"),sQuery(id+"F2.wireOp",EDGE,"E7")])]}),"instanceName":"128"});
            var Q132;
            Q132=makeQuery(id+"F4.opPattern","COPY",BODY,{"derivedFrom":makeQuery(id+"F3.opExtrude","SWEPT_BODY",BODY,{"disambiguationData":[OSD([sQuery(id+"F2.wireOp",EDGE,"E2"),sQuery(id+"F2.wireOp",EDGE,"E3"),sQuery(id+"F2.wireOp",EDGE,"E4"),sQuery(id+"F2.wireOp",EDGE,"E5"),sQuery(id+"F2.wireOp",EDGE,"E6"),sQuery(id+"F2.wireOp",EDGE,"E7")])]}),"instanceName":"129"});
            var Q133;
            Q133=makeQuery(id+"F4.opPattern","COPY",BODY,{"derivedFrom":makeQuery(id+"F3.opExtrude","SWEPT_BODY",BODY,{"disambiguationData":[OSD([sQuery(id+"F2.wireOp",EDGE,"E2"),sQuery(id+"F2.wireOp",EDGE,"E3"),sQuery(id+"F2.wireOp",EDGE,"E4"),sQuery(id+"F2.wireOp",EDGE,"E5"),sQuery(id+"F2.wireOp",EDGE,"E6"),sQuery(id+"F2.wireOp",EDGE,"E7")])]}),"instanceName":"130"});
            var Q134;
            Q134=makeQuery(id+"F4.opPattern","COPY",BODY,{"derivedFrom":makeQuery(id+"F3.opExtrude","SWEPT_BODY",BODY,{"disambiguationData":[OSD([sQuery(id+"F2.wireOp",EDGE,"E2"),sQuery(id+"F2.wireOp",EDGE,"E3"),sQuery(id+"F2.wireOp",EDGE,"E4"),sQuery(id+"F2.wireOp",EDGE,"E5"),sQuery(id+"F2.wireOp",EDGE,"E6"),sQuery(id+"F2.wireOp",EDGE,"E7")])]}),"instanceName":"131"});
            var Q135;
            Q135=makeQuery(id+"F4.opPattern","COPY",BODY,{"derivedFrom":makeQuery(id+"F3.opExtrude","SWEPT_BODY",BODY,{"disambiguationData":[OSD([sQuery(id+"F2.wireOp",EDGE,"E2"),sQuery(id+"F2.wireOp",EDGE,"E3"),sQuery(id+"F2.wireOp",EDGE,"E4"),sQuery(id+"F2.wireOp",EDGE,"E5"),sQuery(id+"F2.wireOp",EDGE,"E6"),sQuery(id+"F2.wireOp",EDGE,"E7")])]}),"instanceName":"132"});
            var Q136;
            Q136=makeQuery(id+"F4.opPattern","COPY",BODY,{"derivedFrom":makeQuery(id+"F3.opExtrude","SWEPT_BODY",BODY,{"disambiguationData":[OSD([sQuery(id+"F2.wireOp",EDGE,"E2"),sQuery(id+"F2.wireOp",EDGE,"E3"),sQuery(id+"F2.wireOp",EDGE,"E4"),sQuery(id+"F2.wireOp",EDGE,"E5"),sQuery(id+"F2.wireOp",EDGE,"E6"),sQuery(id+"F2.wireOp",EDGE,"E7")])]}),"instanceName":"133"});
            var Q137;
            Q137=makeQuery(id+"F4.opPattern","COPY",BODY,{"derivedFrom":makeQuery(id+"F3.opExtrude","SWEPT_BODY",BODY,{"disambiguationData":[OSD([sQuery(id+"F2.wireOp",EDGE,"E2"),sQuery(id+"F2.wireOp",EDGE,"E3"),sQuery(id+"F2.wireOp",EDGE,"E4"),sQuery(id+"F2.wireOp",EDGE,"E5"),sQuery(id+"F2.wireOp",EDGE,"E6"),sQuery(id+"F2.wireOp",EDGE,"E7")])]}),"instanceName":"134"});
            var Q138;
            Q138=makeQuery(id+"F4.opPattern","COPY",BODY,{"derivedFrom":makeQuery(id+"F3.opExtrude","SWEPT_BODY",BODY,{"disambiguationData":[OSD([sQuery(id+"F2.wireOp",EDGE,"E2"),sQuery(id+"F2.wireOp",EDGE,"E3"),sQuery(id+"F2.wireOp",EDGE,"E4"),sQuery(id+"F2.wireOp",EDGE,"E5"),sQuery(id+"F2.wireOp",EDGE,"E6"),sQuery(id+"F2.wireOp",EDGE,"E7")])]}),"instanceName":"135"});
            var Q139;
            Q139=makeQuery(id+"F4.opPattern","COPY",BODY,{"derivedFrom":makeQuery(id+"F3.opExtrude","SWEPT_BODY",BODY,{"disambiguationData":[OSD([sQuery(id+"F2.wireOp",EDGE,"E2"),sQuery(id+"F2.wireOp",EDGE,"E3"),sQuery(id+"F2.wireOp",EDGE,"E4"),sQuery(id+"F2.wireOp",EDGE,"E5"),sQuery(id+"F2.wireOp",EDGE,"E6"),sQuery(id+"F2.wireOp",EDGE,"E7")])]}),"instanceName":"136"});
            var Q140;
            Q140=makeQuery(id+"F4.opPattern","COPY",BODY,{"derivedFrom":makeQuery(id+"F3.opExtrude","SWEPT_BODY",BODY,{"disambiguationData":[OSD([sQuery(id+"F2.wireOp",EDGE,"E2"),sQuery(id+"F2.wireOp",EDGE,"E3"),sQuery(id+"F2.wireOp",EDGE,"E4"),sQuery(id+"F2.wireOp",EDGE,"E5"),sQuery(id+"F2.wireOp",EDGE,"E6"),sQuery(id+"F2.wireOp",EDGE,"E7")])]}),"instanceName":"137"});
            var Q141;
            Q141=makeQuery(id+"F4.opPattern","COPY",BODY,{"derivedFrom":makeQuery(id+"F3.opExtrude","SWEPT_BODY",BODY,{"disambiguationData":[OSD([sQuery(id+"F2.wireOp",EDGE,"E2"),sQuery(id+"F2.wireOp",EDGE,"E3"),sQuery(id+"F2.wireOp",EDGE,"E4"),sQuery(id+"F2.wireOp",EDGE,"E5"),sQuery(id+"F2.wireOp",EDGE,"E6"),sQuery(id+"F2.wireOp",EDGE,"E7")])]}),"instanceName":"138"});
            var Q142;
            Q142=makeQuery(id+"F4.opPattern","COPY",BODY,{"derivedFrom":makeQuery(id+"F3.opExtrude","SWEPT_BODY",BODY,{"disambiguationData":[OSD([sQuery(id+"F2.wireOp",EDGE,"E2"),sQuery(id+"F2.wireOp",EDGE,"E3"),sQuery(id+"F2.wireOp",EDGE,"E4"),sQuery(id+"F2.wireOp",EDGE,"E5"),sQuery(id+"F2.wireOp",EDGE,"E6"),sQuery(id+"F2.wireOp",EDGE,"E7")])]}),"instanceName":"139"});
            var Q143;
            Q143=makeQuery(id+"F4.opPattern","COPY",BODY,{"derivedFrom":makeQuery(id+"F3.opExtrude","SWEPT_BODY",BODY,{"disambiguationData":[OSD([sQuery(id+"F2.wireOp",EDGE,"E2"),sQuery(id+"F2.wireOp",EDGE,"E3"),sQuery(id+"F2.wireOp",EDGE,"E4"),sQuery(id+"F2.wireOp",EDGE,"E5"),sQuery(id+"F2.wireOp",EDGE,"E6"),sQuery(id+"F2.wireOp",EDGE,"E7")])]}),"instanceName":"140"});
            var Q144;
            Q144=makeQuery(id+"F4.opPattern","COPY",BODY,{"derivedFrom":makeQuery(id+"F3.opExtrude","SWEPT_BODY",BODY,{"disambiguationData":[OSD([sQuery(id+"F2.wireOp",EDGE,"E2"),sQuery(id+"F2.wireOp",EDGE,"E3"),sQuery(id+"F2.wireOp",EDGE,"E4"),sQuery(id+"F2.wireOp",EDGE,"E5"),sQuery(id+"F2.wireOp",EDGE,"E6"),sQuery(id+"F2.wireOp",EDGE,"E7")])]}),"instanceName":"141"});
            var Q145;
            Q145=makeQuery(id+"F4.opPattern","COPY",BODY,{"derivedFrom":makeQuery(id+"F3.opExtrude","SWEPT_BODY",BODY,{"disambiguationData":[OSD([sQuery(id+"F2.wireOp",EDGE,"E2"),sQuery(id+"F2.wireOp",EDGE,"E3"),sQuery(id+"F2.wireOp",EDGE,"E4"),sQuery(id+"F2.wireOp",EDGE,"E5"),sQuery(id+"F2.wireOp",EDGE,"E6"),sQuery(id+"F2.wireOp",EDGE,"E7")])]}),"instanceName":"142"});
            var Q146;
            Q146=makeQuery(id+"F4.opPattern","COPY",BODY,{"derivedFrom":makeQuery(id+"F3.opExtrude","SWEPT_BODY",BODY,{"disambiguationData":[OSD([sQuery(id+"F2.wireOp",EDGE,"E2"),sQuery(id+"F2.wireOp",EDGE,"E3"),sQuery(id+"F2.wireOp",EDGE,"E4"),sQuery(id+"F2.wireOp",EDGE,"E5"),sQuery(id+"F2.wireOp",EDGE,"E6"),sQuery(id+"F2.wireOp",EDGE,"E7")])]}),"instanceName":"143"});
            var Q147;
            Q147=makeQuery(id+"F4.opPattern","COPY",BODY,{"derivedFrom":makeQuery(id+"F3.opExtrude","SWEPT_BODY",BODY,{"disambiguationData":[OSD([sQuery(id+"F2.wireOp",EDGE,"E2"),sQuery(id+"F2.wireOp",EDGE,"E3"),sQuery(id+"F2.wireOp",EDGE,"E4"),sQuery(id+"F2.wireOp",EDGE,"E5"),sQuery(id+"F2.wireOp",EDGE,"E6"),sQuery(id+"F2.wireOp",EDGE,"E7")])]}),"instanceName":"144"});
            var Q148;
            Q148=makeQuery(id+"F4.opPattern","COPY",BODY,{"derivedFrom":makeQuery(id+"F3.opExtrude","SWEPT_BODY",BODY,{"disambiguationData":[OSD([sQuery(id+"F2.wireOp",EDGE,"E2"),sQuery(id+"F2.wireOp",EDGE,"E3"),sQuery(id+"F2.wireOp",EDGE,"E4"),sQuery(id+"F2.wireOp",EDGE,"E5"),sQuery(id+"F2.wireOp",EDGE,"E6"),sQuery(id+"F2.wireOp",EDGE,"E7")])]}),"instanceName":"145"});
            var Q149;
            Q149=makeQuery(id+"F4.opPattern","COPY",BODY,{"derivedFrom":makeQuery(id+"F3.opExtrude","SWEPT_BODY",BODY,{"disambiguationData":[OSD([sQuery(id+"F2.wireOp",EDGE,"E2"),sQuery(id+"F2.wireOp",EDGE,"E3"),sQuery(id+"F2.wireOp",EDGE,"E4"),sQuery(id+"F2.wireOp",EDGE,"E5"),sQuery(id+"F2.wireOp",EDGE,"E6"),sQuery(id+"F2.wireOp",EDGE,"E7")])]}),"instanceName":"146"});
            var Q150;
            Q150=makeQuery(id+"F1.opExtrude","SWEPT_BODY",BODY,{"disambiguationData":[OSD([sQuery(id+"F0.wireOp",EDGE,"E0"),sQuery(id+"F0.wireOp",EDGE,"E1")])]});
            booleanBodies(context, id + "F5", {"operationType" : BooleanOperationType.SUBTRACTION, "tools" : qUnion([Q0, Q1, Q2, Q3, Q4, Q5, Q6, Q7, Q8, Q9, Q10, Q11, Q12, Q13, Q14, Q15, Q16, Q17, Q18, Q19, Q20, Q21, Q22, Q23, Q24, Q25, Q26, Q27, Q28, Q29, Q30, Q31, Q32, Q33, Q34, Q35, Q36, Q37, Q38, Q39, Q40, Q41, Q42, Q43, Q44, Q45, Q46, Q47, Q48, Q49, Q50, Q51, Q52, Q53, Q54, Q55, Q56, Q57, Q58, Q59, Q60, Q61, Q62, Q63, Q64, Q65, Q66, Q67, Q68, Q69, Q70, Q71, Q72, Q73, Q74, Q75, Q76, Q77, Q78, Q79, Q80, Q81, Q82, Q83, Q84, Q85, Q86, Q87, Q88, Q89, Q90, Q91, Q92, Q93, Q94, Q95, Q96, Q97, Q98, Q99, Q100, Q101, Q102, Q103, Q104, Q105, Q106, Q107, Q108, Q109, Q110, Q111, Q112, Q113, Q114, Q115, Q116, Q117, Q118, Q119, Q120, Q121, Q122, Q123, Q124, Q125, Q126, Q127, Q128, Q129, Q130, Q131, Q132, Q133, Q134, Q135, Q136, Q137, Q138, Q139, Q140, Q141, Q142, Q143, Q144, Q145, Q146, Q147, Q148, Q149]), "targets" : qUnion([Q150])});
        }
        {
            var Q0;
            Q0=makeQuery(id+"F1.opExtrude","SWEPT_BODY",BODY,{"disambiguationData":[OSD([sQuery(id+"F0.wireOp",EDGE,"E0"),sQuery(id+"F0.wireOp",EDGE,"E1")])]});
            var Q1;
            Q1=sQuery(id+"F0.wireOp",VERTEX,"E0.center");
            transform(context, id + "F6", {"entities" : qUnion([Q0]), "transformType" : TransformType.SCALE_UNIFORMLY, "scale" : 2.6, "scalePoint" : qUnion([Q1]), "makeCopy" : false});
        }
    });
